# Revit family: ВДО
name_source: partatom
category: Оборудование
units: mm (PartAtom-declared; Revit-internal decimal feet)

## family parameters
Всегда вертикально = Да
Классификация = Нет
На основе рабочей плоскости = Нет
Общий = Нет
При загрузке вырезать с полостями = Нет
Размер круглого соединителя = Использовать диаметр
Тип детали = Нормальный
Точка принадлежности помещению = Нет

## types (239) — shared parameters
00_20_Manufacturer = Вентс
00_20_Name = Осьовий вентилятор димовидалення
Casing Material = Металл, окрашенный, синий, матовый RAL 5007
Grid Material = Cover Grid Cross
Load Classification = HVAC
Maintenance zone material = <По категории>
Number of Fase = 3
Voltage = 400 В
Струм = 0 А
zero-valued in all types: Отметка по умолчанию

## per-type parameters (varying)
| type | 00_20_Type | D1 | D2 | Dn | Dv | Dy | L | Ld | Lv | Maximum Air Flow | N | P | Power | W | W1 | d | l | l1 | n | r1 | Вага | Двигатель |
| ВДО-400-2Д/0,55-6/25/AЛ | ВДО-400-2Д/0,55-6/25/AЛ | 450 мм | 490 мм | 404 мм | 390 мм | 400 мм | 400 мм | 120 мм | 105 мм | 1390.0 л/с | 6 | 240 мм | 550 Вт | 525 мм | 475 мм | 8 мм | 200 мм | -200 мм | 12 | 225 мм | 23.00 кг | Двигатель : Двигатель_0.55 кВт |
| ВДО-1250-4Д/18,5-8/23/AЛ | ВДО-1250-4Д/18,5-8/23/AЛ | 1320 мм | 1400 мм | 1254 мм | 1240 мм | 1250 мм | 750 мм | 225 мм | 210 мм | 21400.0 л/с | 8 | 665 мм | 18500 Вт | 1450 мм | 1400 мм | 15 мм | 375 мм | -375 мм | 20 | 660 мм | 335.00 кг | Двигатель : Двигатель_18.5 кВт |
| ВДО-500-2Д/1,1-6/25/AЛ | ВДО-500-2Д/1,1-6/25/AЛ | 560 мм | 600 мм | 504 мм | 490 мм | 500 мм | 400 мм | 120 мм | 105 мм | 2200.0 л/с | 6 | 290 мм | 1100 Вт | 620 мм | 570 мм | 12 мм | 200 мм | -200 мм | 12 | 280 мм | 32.00 кг | Двигатель : Двигатель_1.1 кВт |
| ВДО-560-2Д/1,1-6/25/AЛ | ВДО-560-2Д/1,1-6/25/AЛ | 620 мм | 660 мм | 564 мм | 550 мм | 560 мм | 400 мм | 120 мм | 105 мм | 2650.0 л/с | 6 | 320 мм | 1100 Вт | 680 мм | 630 мм | 12 мм | 200 мм | -200 мм | 12 | 310 мм | 34.00 кг | Двигатель : Двигатель_1.1 кВт |
| ВДО-450-2Д/0,75-6/25/AЛ | ВДО-450-2Д/0,75-6/25/AЛ | 500 мм | 540 мм | 454 мм | 440 мм | 450 мм | 400 мм | 120 мм | 105 мм | 1800.0 л/с | 6 | 265 мм | 750 Вт | 580 мм | 530 мм | 8 мм | 200 мм | -200 мм | 12 | 250 мм | 26.10 кг | Двигатель : Двигатель_0.75 кВт |
| ВДО-630-2Д/2,2-6/25/AЛ | ВДО-630-2Д/2,2-6/25/AЛ | 620 мм | 690 мм | 634 мм | 620 мм | 630 мм | 400 мм | 120 мм | 105 мм | 3900.0 л/с | 6 | 355 мм | 2200 Вт | 750 мм | 700 мм | 12 мм | 200 мм | -200 мм | 12 | 310 мм | 41.50 кг | Двигатель : Двигатель_2.2 кВт |
| ВДО-710-4Д/0,75-6/20/AЛ | ВДО-710-4Д/0,75-6/20/AЛ | 770 мм | 810 мм | 714 мм | 700 мм | 710 мм | 400 мм | 120 мм | 105 мм | 2900.0 л/с | 6 | 395 мм | 750 Вт | 845 мм | 795 мм | 12 мм | 200 мм | -200 мм | 16 | 385 мм | 47.50 кг | Двигатель : Двигатель_0.75 кВт |
| ВДО-800-4Д/1,1-6/20/AЛ | ВДО-800-4Д/1,1-6/20/AЛ | 860 мм | 900 мм | 804 мм | 790 мм | 800 мм | 400 мм | 120 мм | 105 мм | 3900.0 л/с | 6 | 440 мм | 1100 Вт | 925 мм | 875 мм | 12 мм | 200 мм | -200 мм | 16 | 430 мм | 59.50 кг | Двигатель : Двигатель_1.1 кВт |
| ВДО-900-4Д/3-8/23,5/AЛ | ВДО-900-4Д/3-8/23,5/AЛ | 970 мм | 1015 мм | 904 мм | 890 мм | 900 мм | 550 мм | 165 мм | 150 мм | 6500.0 л/с | 8 | 490 мм | 3000 Вт | 1025 мм | 975 мм | 15 мм | 275 мм | -275 мм | 16 | 485 мм | 92.00 кг | Двигатель : Двигатель_3 кВт |
| ВДО-1000-4Д/5,5-6/24/AЛ | ВДО-1000-4Д/5,5-6/24/AЛ | 1070 мм | 1115 мм | 1004 мм | 990 мм | 1000 мм | 600 мм | 180 мм | 165 мм | 10000.0 л/с | 6 | 540 мм | 5500 Вт | 1140 мм | 1090 мм | 15 мм | 300 мм | -300 мм | 16 | 535 мм | 147.50 кг | Двигатель : Двигатель_5.5 кВт |
| ВДО-1120-4Д/7,5-6/23/AЛ | ВДО-1120-4Д/7,5-6/23/AЛ | 1190 мм | 1270 мм | 1124 мм | 1110 мм | 1120 мм | 600 мм | 180 мм | 165 мм | 13000.0 л/с | 6 | 600 мм | 7500 Вт | 1280 мм | 1230 мм | 15 мм | 300 мм | -300 мм | 20 | 595 мм | 183.00 кг | Двигатель : Двигатель_7.5 кВт |
| ВДО-400-2Д/0,75-6/30/AЛ | ВДО-400-2Д/0,75-6/30/AЛ | 450 мм | 490 мм | 404 мм | 390 мм | 400 мм | 400 мм | 120 мм | 105 мм | 1600.0 л/с | 6 | 240 мм | 750 Вт | 525 мм | 475 мм | 8 мм | 200 мм | -200 мм | 12 | 225 мм | 24.60 кг | Двигатель : Двигатель_0.75 кВт |
| ВДО-400-2Д/1,1-6/35/AЛ | ВДО-400-2Д/1,1-6/35/AЛ | 450 мм | 490 мм | 404 мм | 390 мм | 400 мм | 400 мм | 120 мм | 105 мм | 1850.0 л/с | 6 | 240 мм | 1100 Вт | 525 мм | 475 мм | 8 мм | 200 мм | -200 мм | 12 | 225 мм | 28.60 кг | Двигатель : Двигатель_1.1 кВт |
| ВДО-400-2Д/1,5-6/40/AЛ | ВДО-400-2Д/1,5-6/40/AЛ | 450 мм | 490 мм | 404 мм | 390 мм | 400 мм | 400 мм | 120 мм | 105 мм | 2000.0 л/с | 6 | 240 мм | 1500 Вт | 525 мм | 475 мм | 8 мм | 200 мм | -200 мм | 12 | 225 мм | 30.10 кг | Двигатель : Двигатель_1.5 кВт |
| ВДО-400-2Д/1,5-6/45/AЛ | ВДО-400-2Д/1,5-6/45/AЛ | 450 мм | 490 мм | 404 мм | 390 мм | 400 мм | 400 мм | 120 мм | 105 мм | 2200.0 л/с | 6 | 240 мм | 1500 Вт | 525 мм | 475 мм | 8 мм | 200 мм | -200 мм | 12 | 225 мм | 30.10 кг | Двигатель : Двигатель_1.5 кВт |
| ВДО-400-2Д/2,2-8/45/AЛ | ВДО-400-2Д/2,2-8/45/AЛ | 450 мм | 490 мм | 404 мм | 390 мм | 400 мм | 400 мм | 120 мм | 105 мм | 2300.0 л/с | 8 | 240 мм | 2200 Вт | 525 мм | 475 мм | 8 мм | 200 мм | -200 мм | 12 | 225 мм | 32.60 кг | Двигатель : Двигатель_2.2 кВт |
| ВДО-400-4Д/0,55-6/30/AЛ | ВДО-400-4Д/0,55-6/30/AЛ | 450 мм | 490 мм | 404 мм | 390 мм | 400 мм | 400 мм | 120 мм | 105 мм | 800.0 л/с | 6 | 240 мм | 550 Вт | 525 мм | 475 мм | 8 мм | 200 мм | -200 мм | 12 | 225 мм | 24.50 кг | Двигатель : Двигатель_0.55 кВт |
| ВДО-400-4Д/0,55-6/35/AЛ | ВДО-400-4Д/0,55-6/35/AЛ | 450 мм | 490 мм | 404 мм | 390 мм | 400 мм | 400 мм | 120 мм | 105 мм | 950.0 л/с | 6 | 240 мм | 550 Вт | 525 мм | 475 мм | 8 мм | 200 мм | -200 мм | 12 | 225 мм | 24.50 кг | Двигатель : Двигатель_0.55 кВт |
| ВДО-400-4Д/0,55-6/40/AЛ | ВДО-400-4Д/0,55-6/40/AЛ | 450 мм | 490 мм | 404 мм | 390 мм | 400 мм | 400 мм | 120 мм | 105 мм | 1000.0 л/с | 6 | 240 мм | 550 Вт | 525 мм | 475 мм | 8 мм | 200 мм | -200 мм | 12 | 225 мм | 24.50 кг | Двигатель : Двигатель_0.55 кВт |
| ВДО-400-4Д/0,55-6/45/AЛ | ВДО-400-4Д/0,55-6/45/AЛ | 450 мм | 490 мм | 404 мм | 390 мм | 400 мм | 400 мм | 120 мм | 105 мм | 1050.0 л/с | 6 | 240 мм | 550 Вт | 525 мм | 475 мм | 8 мм | 200 мм | -200 мм | 12 | 225 мм | 24.50 кг | Двигатель : Двигатель_0.55 кВт |
| ВДО-400-4Д/0,55-8/45/AЛ | ВДО-400-4Д/0,55-8/45/AЛ | 450 мм | 490 мм | 404 мм | 390 мм | 400 мм | 400 мм | 120 мм | 105 мм | 1150.0 л/с | 8 | 240 мм | 550 Вт | 525 мм | 475 мм | 8 мм | 200 мм | -200 мм | 12 | 225 мм | 25.00 кг | Двигатель : Двигатель_0.55 кВт |
| ВДО-400-2/4Д/0,8/0,2-6/30/AЛ | ВДО-400-2/4Д/0,8/0,2-6/30/AЛ | 450 мм | 490 мм | 404 мм | 390 мм | 400 мм | 400 мм | 120 мм | 105 мм | 1600.0 л/с | 6 | 240 мм | 800 Вт | 525 мм | 475 мм | 8 мм | 200 мм | -200 мм | 12 | 225 мм | 29.10 кг | Двигатель : Двигатель_0.8 кВт |
| ВДО-400-2/4Д/1,1/0,25-6/35/AЛ | ВДО-400-2/4Д/1,1/0,25-6/35/AЛ | 450 мм | 490 мм | 404 мм | 390 мм | 400 мм | 400 мм | 120 мм | 105 мм | 1850.0 л/с | 6 | 240 мм | 1100 Вт | 525 мм | 475 мм | 8 мм | 200 мм | -200 мм | 12 | 225 мм | 30.10 кг | Двигатель : Двигатель_1.1 кВт |
| ВДО-400-2/4Д/1,5/0,37-6/40/AЛ | ВДО-400-2/4Д/1,5/0,37-6/40/AЛ | 450 мм | 490 мм | 404 мм | 390 мм | 400 мм | 400 мм | 120 мм | 105 мм | 2000.0 л/с | 6 | 240 мм | 1100 Вт | 525 мм | 475 мм | 8 мм | 200 мм | -200 мм | 12 | 225 мм | 35.80 кг | Двигатель : Двигатель_1.5 кВт |
| ВДО-400-2/4Д/1,5/0,37-6/45/AЛ | ВДО-400-2/4Д/1,5/0,37-6/45/AЛ | 450 мм | 490 мм | 404 мм | 390 мм | 400 мм | 400 мм | 120 мм | 105 мм | 2200.0 л/с | 6 | 240 мм | 1500 Вт | 525 мм | 475 мм | 8 мм | 200 мм | -200 мм | 12 | 225 мм | 35.80 кг | Двигатель : Двигатель_1.5 кВт |
| ВДО-400-2/4Д/2,2/0,5-8/45/AЛ | ВДО-400-2/4Д/2,2/0,5-8/45/AЛ | 450 мм | 490 мм | 404 мм | 390 мм | 400 мм | 400 мм | 120 мм | 105 мм | 2250.0 л/с | 8 | 240 мм | 2200 Вт | 525 мм | 475 мм | 8 мм | 200 мм | -200 мм | 12 | 225 мм | 38.00 кг | Двигатель : Двигатель_2.2 кВт |
| ВДО-450-2Д/1,1-6/30/AЛ | ВДО-450-2Д/1,1-6/30/AЛ | 500 мм | 540 мм | 454 мм | 440 мм | 450 мм | 400 мм | 120 мм | 105 мм | 2170.0 л/с | 6 | 265 мм | 1100 Вт | 580 мм | 530 мм | 8 мм | 200 мм | -200 мм | 12 | 250 мм | 30.10 кг | Двигатель : Двигатель_1.1 кВт |
| ВДО-450-2Д/1,5-6/35/AЛ | ВДО-450-2Д/1,5-6/35/AЛ | 500 мм | 540 мм | 454 мм | 440 мм | 450 мм | 400 мм | 120 мм | 105 мм | 2600.0 л/с | 6 | 265 мм | 1500 Вт | 580 мм | 530 мм | 8 мм | 200 мм | -200 мм | 12 | 250 мм | 31.60 кг | Двигатель : Двигатель_1.5 кВт |
| ВДО-450-2Д/2,2-6/40/AЛ | ВДО-450-2Д/2,2-6/40/AЛ | 500 мм | 540 мм | 454 мм | 440 мм | 450 мм | 400 мм | 120 мм | 105 мм | 2800.0 л/с | 6 | 265 мм | 2200 Вт | 580 мм | 530 мм | 8 мм | 200 мм | -200 мм | 12 | 250 мм | 34.00 кг | Двигатель : Двигатель_2.2 кВт |
| ВДО-450-2Д/3-8/40/AЛ | ВДО-450-2Д/3-8/40/AЛ | 500 мм | 540 мм | 454 мм | 440 мм | 450 мм | 400 мм | 120 мм | 105 мм | 2900.0 л/с | 6 | 265 мм | 3000 Вт | 580 мм | 530 мм | 8 мм | 200 мм | -200 мм | 12 | 250 мм | 34.00 кг | Двигатель : Двигатель_3 кВт |
| ВДО-450-2Д/4-8/45/AЛ | ВДО-450-2Д/4-8/45/AЛ | 500 мм | 540 мм | 454 мм | 440 мм | 450 мм | 400 мм | 120 мм | 105 мм | 3300.0 л/с | 8 | 265 мм | 4000 Вт | 580 мм | 530 мм | 8 мм | 200 мм | -200 мм | 12 | 250 мм | 52.80 кг | Двигатель : Двигатель_3 кВт |
| ВДО-450-4Д/0,55-6/25/AЛ | ВДО-450-2Д/3-8/40/AЛ | 500 мм | 540 мм | 454 мм | 440 мм | 450 мм | 400 мм | 120 мм | 105 мм | 640.0 л/с | 6 | 265 мм | 550 Вт | 580 мм | 530 мм | 8 мм | 200 мм | -200 мм | 12 | 250 мм | 24.60 кг | Двигатель : Двигатель_0.55 кВт |
| ВДО-450-4Д/0,55-6/30/AЛ | ВДО-450-4Д/0,55-6/30/AЛ | 500 мм | 540 мм | 454 мм | 440 мм | 450 мм | 400 мм | 120 мм | 105 мм | 1050.0 л/с | 6 | 265 мм | 550 Вт | 580 мм | 530 мм | 8 мм | 200 мм | -200 мм | 12 | 250 мм | 24.60 кг | Двигатель : Двигатель_0.55 кВт |
| ВДО-450-4Д/0,55-6/35/AЛ | ВДО-450-4Д/0,55-6/35/AЛ | 500 мм | 540 мм | 454 мм | 440 мм | 450 мм | 400 мм | 120 мм | 105 мм | 1250.0 л/с | 6 | 265 мм | 550 Вт | 580 мм | 530 мм | 8 мм | 200 мм | -200 мм | 12 | 250 мм | 24.60 кг | Двигатель : Двигатель_0.55 кВт |
| ВДО-450-4Д/0,55-6/40/AЛ | ВДО-450-4Д/0,55-6/40/AЛ | 500 мм | 540 мм | 454 мм | 440 мм | 450 мм | 400 мм | 120 мм | 105 мм | 1400.0 л/с | 6 | 265 мм | 550 Вт | 580 мм | 530 мм | 8 мм | 200 мм | -200 мм | 12 | 250 мм | 24.60 кг | Двигатель : Двигатель_0.55 кВт |
| ВДО-450-4Д/0,55-8/40/AЛ | ВДО-450-4Д/0,55-8/40/AЛ | 500 мм | 540 мм | 454 мм | 440 мм | 450 мм | 400 мм | 120 мм | 105 мм | 1450.0 л/с | 8 | 265 мм | 550 Вт | 580 мм | 530 мм | 8 мм | 200 мм | -200 мм | 12 | 250 мм | 24.60 кг | Двигатель : Двигатель_0.55 кВт |
| ВДО-450-4Д/0,55-8/45/AЛ | ВДО-450-4Д/0,55-8/45/AЛ | 500 мм | 540 мм | 454 мм | 440 мм | 450 мм | 400 мм | 120 мм | 105 мм | 1650.0 л/с | 8 | 265 мм | 550 Вт | 580 мм | 530 мм | 8 мм | 200 мм | -200 мм | 12 | 250 мм | 24.60 кг | Двигатель : Двигатель_0.55 кВт |
| ВДО-450-2/4Д/4,4/1,1-8/45/AЛ | ВДО-450-2/4Д/4,4/1,1-8/45/AЛ | 500 мм | 540 мм | 454 мм | 440 мм | 450 мм | 400 мм | 120 мм | 105 мм | 3300.0 л/с | 8 | 265 мм | 4400 Вт | 580 мм | 530 мм | 8 мм | 200 мм | -200 мм | 12 | 250 мм | 63.80 кг | Двигатель : Двигатель_4.4 кВт |
| ВДО-450-2/4Д/3,1/0,8-8/40/AЛ | ВДО-450-2/4Д/3,1/0,8-8/40/AЛ | 500 мм | 540 мм | 454 мм | 440 мм | 450 мм | 400 мм | 120 мм | 105 мм | 2900.0 л/с | 8 | 265 мм | 3100 Вт | 580 мм | 530 мм | 8 мм | 200 мм | -200 мм | 12 | 250 мм | 51.90 кг | Двигатель : Двигатель_3.1 кВт |
| ВДО-450-2/4Д/2,2/0,5-6/40/AЛ | ВДО-450-2/4Д/2,2/0,5-6/40/AЛ | 500 мм | 540 мм | 454 мм | 440 мм | 450 мм | 400 мм | 120 мм | 105 мм | 2800.0 л/с | 6 | 265 мм | 2200 Вт | 580 мм | 530 мм | 8 мм | 200 мм | -200 мм | 12 | 250 мм | 39.30 кг | Двигатель : Двигатель_2.2 кВт |
| ВДО-450-2/4Д/1,5/0,37-6/35/AЛ | ВДО-450-2/4Д/1,5/0,37-6/35/AЛ | 500 мм | 540 мм | 454 мм | 440 мм | 450 мм | 400 мм | 120 мм | 105 мм | 2500.0 л/с | 6 | 265 мм | 1500 Вт | 580 мм | 530 мм | 8 мм | 200 мм | -200 мм | 12 | 250 мм | 37.30 кг | Двигатель : Двигатель_1.5 кВт |
| ВДО-450-2/4Д/1,1/0,25-6/30/AЛ | ВДО-450-2/4Д/1,1/0,25-6/30/AЛ | 500 мм | 540 мм | 454 мм | 440 мм | 450 мм | 400 мм | 120 мм | 105 мм | 2150.0 л/с | 6 | 265 мм | 1100 Вт | 580 мм | 530 мм | 8 мм | 200 мм | -200 мм | 12 | 250 мм | 31.60 кг | Двигатель : Двигатель_1.1 кВт |
| ВДО-450-2/4Д/0,8/0,2-6/25/AЛ | ВДО-450-2/4Д/0,8/0,2-6/25/AЛ | 500 мм | 540 мм | 454 мм | 440 мм | 450 мм | 400 мм | 120 мм | 105 мм | 1800.0 л/с | 6 | 265 мм | 800 Вт | 580 мм | 530 мм | 8 мм | 200 мм | -200 мм | 12 | 250 мм | 30.60 кг | Двигатель : Двигатель_0.8 кВт |
| ВДО-500-2Д/1,5-6/30/AЛ | ВДО-500-2Д/1,5-6/30/AЛ | 560 мм | 600 мм | 504 мм | 490 мм | 500 мм | 400 мм | 120 мм | 105 мм | 2650.0 л/с | 6 | 290 мм | 1500 Вт | 620 мм | 570 мм | 12 мм | 200 мм | -200 мм | 12 | 280 мм | 33.50 кг | Двигатель : Двигатель_1.5 кВт |
| ВДО-500-2Д/2,2-6/35/AЛ | ВДО-500-2Д/2,2-6/35/AЛ | 560 мм | 600 мм | 504 мм | 490 мм | 500 мм | 400 мм | 120 мм | 105 мм | 3200.0 л/с | 6 | 290 мм | 2200 Вт | 620 мм | 570 мм | 12 мм | 200 мм | -200 мм | 12 | 280 мм | 36.00 кг | Двигатель : Двигатель_2.2 кВт |
| ВДО-500-2Д/3-8/35/AЛ | ВДО-500-2Д/3-8/35/AЛ | 560 мм | 600 мм | 504 мм | 490 мм | 500 мм | 400 мм | 120 мм | 105 мм | 3500.0 л/с | 8 | 290 мм | 3000 Вт | 620 мм | 570 мм | 12 мм | 200 мм | -200 мм | 12 | 280 мм | 43.00 кг | Двигатель : Двигатель_3 кВт |
| ВДО-500-2Д/4-8/40/AЛ | ВДО-500-2Д/4-8/40/AЛ | 560 мм | 600 мм | 504 мм | 490 мм | 500 мм | 500 мм | 150 мм | 135 мм | 3900.0 л/с | 8 | 290 мм | 4000 Вт | 620 мм | 570 мм | 12 мм | 250 мм | -250 мм | 12 | 280 мм | 55.00 кг | Двигатель : Двигатель_4 кВт |
| ВДО-500-2Д/5,5-8/45/AЛ | ВДО-500-2Д/5,5-8/45/AЛ | 560 мм | 600 мм | 504 мм | 490 мм | 500 мм | 500 мм | 150 мм | 135 мм | 4300.0 л/с | 8 | 290 мм | 5500 Вт | 620 мм | 570 мм | 12 мм | 250 мм | -250 мм | 12 | 280 мм | 63.00 кг | Двигатель : Двигатель_5.5 кВт |
| ВДО-500-4Д/0,55-6/25/AЛ | ВДО-500-4Д/0,55-6/25/AЛ | 560 мм | 600 мм | 504 мм | 490 мм | 500 мм | 400 мм | 120 мм | 105 мм | 1100.0 л/с | 6 | 290 мм | 550 Вт | 620 мм | 570 мм | 12 мм | 200 мм | -200 мм | 12 | 280 мм | 28.00 кг | Двигатель : Двигатель_0.55 кВт |
| ВДО-500-4Д/0,55-6/30/AЛ | ВДО-500-4Д/0,55-6/30/AЛ | 560 мм | 600 мм | 504 мм | 490 мм | 500 мм | 400 мм | 120 мм | 105 мм | 1350.0 л/с | 6 | 290 мм | 550 Вт | 620 мм | 570 мм | 12 мм | 200 мм | -200 мм | 12 | 280 мм | 28.00 кг | Двигатель : Двигатель_0.55 кВт |
| ВДО-500-4Д/0,55-6/35/AЛ | ВДО-500-4Д/0,55-6/35/AЛ | 560 мм | 600 мм | 504 мм | 490 мм | 500 мм | 400 мм | 120 мм | 105 мм | 1650.0 л/с | 6 | 290 мм | 550 Вт | 620 мм | 570 мм | 12 мм | 200 мм | -200 мм | 12 | 280 мм | 28.00 кг | Двигатель : Двигатель_0.55 кВт |
| ВДО-500-4Д/0,55-6/40/AЛ | ВДО-500-4Д/0,55-6/40/AЛ | 560 мм | 600 мм | 504 мм | 490 мм | 500 мм | 400 мм | 120 мм | 105 мм | 1780.0 л/с | 6 | 290 мм | 550 Вт | 620 мм | 570 мм | 12 мм | 200 мм | -200 мм | 12 | 280 мм | 28.00 кг | Двигатель : Двигатель_0.55 кВт |
| ВДО-500-4Д/0,55-6/45/AЛ | ВДО-500-4Д/0,55-6/45/AЛ | 560 мм | 600 мм | 504 мм | 490 мм | 500 мм | 400 мм | 120 мм | 105 мм | 1950.0 л/с | 6 | 290 мм | 550 Вт | 620 мм | 570 мм | 12 мм | 200 мм | -200 мм | 12 | 280 мм | 28.00 кг | Двигатель : Двигатель_0.55 кВт |
| ВДО-500-4Д/0,75-8/45/AЛ | ВДО-500-4Д/0,75-8/45/AЛ | 560 мм | 600 мм | 504 мм | 490 мм | 500 мм | 400 мм | 120 мм | 105 мм | 2100.0 л/с | 8 | 290 мм | 750 Вт | 620 мм | 570 мм | 12 мм | 200 мм | -200 мм | 12 | 280 мм | 29.50 кг | Двигатель : Двигатель_0.75 кВт |
| ВДО-500-2/4Д/1,1/0,25-6/25/AЛ | ВДО-500-2/4Д/1,1/0,25-6/25/AЛ | 560 мм | 600 мм | 504 мм | 490 мм | 500 мм | 400 мм | 120 мм | 105 мм | 2200.0 л/с | 6 | 290 мм | 1100 Вт | 620 мм | 570 мм | 12 мм | 200 мм | -200 мм | 12 | 280 мм | 29.50 кг | Двигатель : Двигатель_1.1 кВт |
| ВДО-500-2/4Д/1,5/0,37-6/30/AЛ | ВДО-500-2/4Д/1,5/0,37-6/30/AЛ | 560 мм | 600 мм | 504 мм | 490 мм | 500 мм | 400 мм | 120 мм | 105 мм | 2650.0 л/с | 6 | 290 мм | 1500 Вт | 620 мм | 570 мм | 12 мм | 200 мм | -200 мм | 12 | 280 мм | 39.00 кг | Двигатель : Двигатель_1.5 кВт |
| ВДО-500-2/4Д/2,2/0,5-6/35/AЛ | ВДО-500-2/4Д/2,2/0,5-6/35/AЛ | 560 мм | 600 мм | 504 мм | 490 мм | 500 мм | 400 мм | 120 мм | 105 мм | 3200.0 л/с | 6 | 290 мм | 2200 Вт | 620 мм | 570 мм | 12 мм | 200 мм | -200 мм | 12 | 280 мм | 41.00 кг | Двигатель : Двигатель_2.2 кВт |
| ВДО-500-2/4Д/3,1/0,8-8/35/AЛ | ВДО-500-2/4Д/3,1/0,8-8/35/AЛ | 560 мм | 600 мм | 504 мм | 490 мм | 500 мм | 500 мм | 150 мм | 135 мм | 3600.0 л/с | 8 | 290 мм | 3100 Вт | 620 мм | 570 мм | 12 мм | 250 мм | -250 мм | 12 | 280 мм | 54.00 кг | Двигатель : Двигатель_3.1 кВт |
| ВДО-500-2/4Д/4,4/1,1-8/40/AЛ | ВДО-500-2/4Д/4,4/1,1-8/40/AЛ | 560 мм | 600 мм | 504 мм | 490 мм | 500 мм | 500 мм | 150 мм | 135 мм | 3900.0 л/с | 8 | 290 мм | 4400 Вт | 620 мм | 570 мм | 12 мм | 250 мм | -250 мм | 12 | 280 мм | 66.00 кг | Двигатель : Двигатель_4.4 кВт |
| ВДО-500-2/4Д/6/1,5-8/45/AЛ | ВДО-500-2/4Д/6/1,5-8/45/AЛ | 560 мм | 600 мм | 504 мм | 490 мм | 500 мм | 550 мм | 165 мм | 150 мм | 4300.0 л/с | 8 | 290 мм | 6000 Вт | 620 мм | 570 мм | 12 мм | 275 мм | -275 мм | 12 | 280 мм | 85.00 кг | Двигатель : Двигатель_6 кВт |
| ВДО-560-2Д/1,5-6/30/AЛ | ВДО-560-2Д/1,5-6/30/AЛ | 620 мм | 660 мм | 564 мм | 550 мм | 560 мм | 400 мм | 120 мм | 105 мм | 3300.0 л/с | 6 | 320 мм | 1500 Вт | 680 мм | 630 мм | 12 мм | 200 мм | -200 мм | 12 | 310 мм | 35.50 кг | Двигатель : Двигатель_1.5 кВт |
| ВДО-560-2Д/2,2-8/30/AЛ | ВДО-560-2Д/2,2-8/30/AЛ | 620 мм | 660 мм | 564 мм | 550 мм | 560 мм | 400 мм | 120 мм | 105 мм | 3750.0 л/с | 8 | 320 мм | 2200 Вт | 680 мм | 630 мм | 12 мм | 200 мм | -200 мм | 12 | 310 мм | 38.00 кг | Двигатель : Двигатель_2.2 кВт |
| ВДО-560-2Д/4-8/35/AЛ | ВДО-560-2Д/4-8/35/AЛ | 620 мм | 660 мм | 564 мм | 550 мм | 560 мм | 500 мм | 150 мм | 135 мм | 4580.0 л/с | 8 | 320 мм | 4000 Вт | 680 мм | 630 мм | 12 мм | 250 мм | -250 мм | 12 | 310 мм | 57.50 кг | Двигатель : Двигатель_4 кВт |
| ВДО-560-2Д/5,5-8/40/AЛ | ВДО-560-2Д/5,5-8/40/AЛ | 620 мм | 660 мм | 564 мм | 550 мм | 560 мм | 500 мм | 150 мм | 135 мм | 5000.0 л/с | 8 | 320 мм | 5500 Вт | 680 мм | 630 мм | 12 мм | 250 мм | -250 мм | 12 | 310 мм | 65.50 кг | Двигатель : Двигатель_5.5 кВт |
| ВДО-560-2Д/7,5-8/45/AЛ | ВДО-560-2Д/7,5-8/45/AЛ | 620 мм | 660 мм | 564 мм | 550 мм | 560 мм | 500 мм | 150 мм | 135 мм | 5700.0 л/с | 8 | 320 мм | 7500 Вт | 680 мм | 630 мм | 12 мм | 250 мм | -250 мм | 12 | 310 мм | 67.50 кг | Двигатель : Двигатель_7.5 кВт |
| ВДО-560-4Д/0,55-6/25/AЛ | ВДО-560-4Д/0,55-6/25/AЛ | 620 мм | 660 мм | 564 мм | 550 мм | 560 мм | 400 мм | 120 мм | 105 мм | 1350.0 л/с | 6 | 320 мм | 550 Вт | 680 мм | 630 мм | 12 мм | 200 мм | -200 мм | 12 | 310 мм | 30.00 кг | Двигатель : Двигатель_0.55 кВт |
| ВДО-560-4Д/0,55-6/30/AЛ | ВДО-560-4Д/0,55-6/30/AЛ | 620 мм | 660 мм | 564 мм | 550 мм | 560 мм | 400 мм | 120 мм | 105 мм | 1650.0 л/с | 6 | 320 мм | 550 Вт | 680 мм | 630 мм | 12 мм | 200 мм | -200 мм | 12 | 310 мм | 30.00 кг | Двигатель : Двигатель_0.55 кВт |
| ВДО-560-4Д/0,55-6/35/AЛ | ВДО-560-4Д/0,55-6/35/AЛ | 620 мм | 660 мм | 564 мм | 550 мм | 560 мм | 400 мм | 120 мм | 105 мм | 2050.0 л/с | 6 | 320 мм | 550 Вт | 680 мм | 630 мм | 12 мм | 200 мм | -200 мм | 12 | 310 мм | 30.00 кг | Двигатель : Двигатель_0.55 кВт |
| ВДО-560-4Д/0,55-6/40/AЛ | ВДО-560-4Д/0,55-6/40/AЛ | 620 мм | 660 мм | 564 мм | 550 мм | 560 мм | 400 мм | 120 мм | 105 мм | 2300.0 л/с | 6 | 320 мм | 550 Вт | 680 мм | 630 мм | 12 мм | 200 мм | -200 мм | 12 | 310 мм | 30.00 кг | Двигатель : Двигатель_0.55 кВт |
| ВДО-560-4Д/0,55-6/45/AЛ | ВДО-560-4Д/0,55-6/45/AЛ | 620 мм | 660 мм | 564 мм | 550 мм | 560 мм | 400 мм | 120 мм | 105 мм | 2500.0 л/с | 6 | 320 мм | 550 Вт | 680 мм | 630 мм | 12 мм | 200 мм | -200 мм | 12 | 310 мм | 30.00 кг | Двигатель : Двигатель_0.55 кВт |
| ВДО-560-4Д/0,75-8/45/AЛ | ВДО-560-4Д/0,75-8/45/AЛ | 620 мм | 660 мм | 564 мм | 550 мм | 560 мм | 400 мм | 120 мм | 105 мм | 2850.0 л/с | 8 | 320 мм | 750 Вт | 680 мм | 630 мм | 12 мм | 200 мм | -200 мм | 12 | 310 мм | 31.50 кг | Двигатель : Двигатель_0.75 кВт |
| ВДО-560-2/4Д/1,1/0,25-6/25/AЛ | ВДО-560-2/4Д/1,1/0,25-6/25/AЛ | 620 мм | 660 мм | 564 мм | 550 мм | 560 мм | 400 мм | 120 мм | 105 мм | 2700.0 л/с | 6 | 320 мм | 1100 Вт | 680 мм | 630 мм | 12 мм | 200 мм | -200 мм | 12 | 310 мм | 35.50 кг | Двигатель : Двигатель_1.1 кВт |
| ВДО-560-2/4Д/1,5/0,37-6/30/AЛ | ВДО-560-2/4Д/1,5/0,37-6/30/AЛ | 620 мм | 660 мм | 564 мм | 550 мм | 560 мм | 400 мм | 120 мм | 105 мм | 3300.0 л/с | 6 | 320 мм | 1500 Вт | 680 мм | 630 мм | 12 мм | 200 мм | -200 мм | 12 | 310 мм | 41.00 кг | Двигатель : Двигатель_1.5 кВт |
| ВДО-560-2/4Д/2,2/0,5-8/30/AЛ | ВДО-560-2/4Д/2,2/0,5-8/30/AЛ | 620 мм | 660 мм | 564 мм | 550 мм | 560 мм | 400 мм | 120 мм | 105 мм | 3750.0 л/с | 8 | 320 мм | 2200 Вт | 680 мм | 630 мм | 12 мм | 200 мм | -200 мм | 12 | 310 мм | 43.50 кг | Двигатель : Двигатель_2.2 кВт |
| ВДО-560-2/4Д/4,4/1,1-8/35/AЛ | ВДО-560-2/4Д/4,4/1,1-8/35/AЛ | 620 мм | 660 мм | 564 мм | 550 мм | 560 мм | 500 мм | 150 мм | 135 мм | 4600.0 л/с | 8 | 320 мм | 4400 Вт | 680 мм | 630 мм | 12 мм | 250 мм | -250 мм | 12 | 310 мм | 68.50 кг | Двигатель : Двигатель_4.4 кВт |
| ВДО-560-2/4Д/6/1,5-8/40/AЛ | ВДО-560-2/4Д/6/1,5-8/40/AЛ | 620 мм | 660 мм | 564 мм | 550 мм | 560 мм | 550 мм | 165 мм | 150 мм | 5000.0 л/с | 8 | 320 мм | 6000 Вт | 680 мм | 630 мм | 12 мм | 275 мм | -275 мм | 12 | 310 мм | 96.50 кг | Двигатель : Двигатель_6 кВт |
| ВДО-560-2/4Д/8/2-8/45/AЛ | ВДО-560-2/4Д/8/2-8/45/AЛ | 620 мм | 660 мм | 564 мм | 550 мм | 560 мм | 550 мм | 165 мм | 150 мм | 5700.0 л/с | 8 | 320 мм | 8000 Вт | 680 мм | 630 мм | 12 мм | 275 мм | -275 мм | 12 | 310 мм | 105.50 кг | Двигатель : Двигатель_8 кВт |
| ВДО-630-2Д/3-6/30/AЛ | ВДО-630-2Д/3-6/30/AЛ | 620 мм | 690 мм | 634 мм | 620 мм | 630 мм | 400 мм | 120 мм | 105 мм | 4700.0 л/с | 6 | 355 мм | 3000 Вт | 750 мм | 700 мм | 12 мм | 200 мм | -200 мм | 12 | 310 мм | 48.00 кг | Двигатель : Двигатель_3 кВт |
| ВДО-630-2Д/4-7/32,5/AЛ | ВДО-630-2Д/4-7/32,5/AЛ | 620 мм | 690 мм | 634 мм | 620 мм | 630 мм | 500 мм | 150 мм | 135 мм | 5250.0 л/с | 7 | 355 мм | 4000 Вт | 750 мм | 700 мм | 12 мм | 250 мм | -250 мм | 12 | 310 мм | 61.50 кг | Двигатель : Двигатель_4 кВт |
| ВДО-630-2Д/5,5-7/35/AЛ | ВДО-630-2Д/5,5-7/35/AЛ | 620 мм | 690 мм | 634 мм | 620 мм | 630 мм | 500 мм | 150 мм | 135 мм | 5850.0 л/с | 7 | 355 мм | 5500 Вт | 750 мм | 700 мм | 12 мм | 250 мм | -250 мм | 12 | 310 мм | 70.00 кг | Двигатель : Двигатель_5.5 кВт |
| ВДО-630-2Д/5,5-7/37,5/AЛ | ВДО-630-2Д/5,5-7/37,5/AЛ | 620 мм | 690 мм | 634 мм | 620 мм | 630 мм | 500 мм | 150 мм | 135 мм | 6100.0 л/с | 7 | 355 мм | 5500 Вт | 750 мм | 700 мм | 12 мм | 250 мм | -250 мм | 12 | 310 мм | 70.00 кг | Двигатель : Двигатель_5.5 кВт |
| ВДО-630-2Д/7,5-7/41,5/AЛ | ВДО-630-2Д/7,5-7/41,5/AЛ | 620 мм | 690 мм | 634 мм | 620 мм | 630 мм | 500 мм | 150 мм | 135 мм | 6100.0 л/с | 7 | 355 мм | 7500 Вт | 750 мм | 700 мм | 12 мм | 250 мм | -250 мм | 12 | 310 мм | 71.50 кг | Двигатель : Двигатель_7.5 кВт |
| ВДО-630-2Д/11-8/41,5/AЛ | ВДО-630-2Д/11-8/41,5/AЛ | 620 мм | 690 мм | 634 мм | 620 мм | 630 мм | 550 мм | 165 мм | 150 мм | 7250.0 л/с | 8 | 355 мм | 11000 Вт | 750 мм | 700 мм | 12 мм | 275 мм | -275 мм | 12 | 310 мм | 119.50 кг | Двигатель : Двигатель_11 кВт |
| ВДО-630-2Д/15-8/46,5/AЛ | ВДО-630-2Д/15-8/46,5/AЛ | 620 мм | 690 мм | 634 мм | 620 мм | 630 мм | 700 мм | 210 мм | 195 мм | 8000.0 л/с | 8 | 355 мм | 15000 Вт | 750 мм | 700 мм | 12 мм | 350 мм | -350 мм | 12 | 310 мм | 167.00 кг | Двигатель : Двигатель_15 кВт |
| ВДО-630-2Д/15-9/48,5/AЛ | ВДО-630-2Д/15-9/48,5/AЛ | 620 мм | 690 мм | 634 мм | 620 мм | 630 мм | 700 мм | 210 мм | 195 мм | 8350.0 л/с | 9 | 355 мм | 15000 Вт | 750 мм | 700 мм | 12 мм | 350 мм | -350 мм | 12 | 310 мм | 166.00 кг | Двигатель : Двигатель_15 кВт |
| ВДО-630-4Д/0,55-8/25/AЛ | ВДО-630-4Д/0,55-8/25/AЛ | 620 мм | 690 мм | 634 мм | 620 мм | 630 мм | 400 мм | 120 мм | 105 мм | 1800.0 л/с | 8 | 355 мм | 550 Вт | 750 мм | 700 мм | 12 мм | 200 мм | -200 мм | 12 | 310 мм | 31.50 кг | Двигатель : Двигатель_0.55 кВт |
| ВДО-630-4Д/0,55-8/30/AЛ | ВДО-630-4Д/0,55-8/30/AЛ | 620 мм | 690 мм | 634 мм | 620 мм | 630 мм | 400 мм | 120 мм | 105 мм | 2300.0 л/с | 8 | 355 мм | 550 Вт | 750 мм | 700 мм | 12 мм | 200 мм | -200 мм | 12 | 310 мм | 31.50 кг | Двигатель : Двигатель_0.55 кВт |
| ВДО-630-4Д/0,75-8/35/AЛ | ВДО-630-4Д/0,75-8/35/AЛ | 620 мм | 690 мм | 634 мм | 620 мм | 630 мм | 400 мм | 120 мм | 105 мм | 2850.0 л/с | 8 | 355 мм | 750 Вт | 750 мм | 700 мм | 12 мм | 200 мм | -200 мм | 12 | 310 мм | 32.50 кг | Двигатель : Двигатель_0.75 кВт |
| ВДО-630-4Д/1,1-8/40/AЛ | ВДО-630-4Д/1,1-8/40/AЛ | 620 мм | 690 мм | 634 мм | 620 мм | 630 мм | 400 мм | 120 мм | 105 мм | 3200.0 л/с | 8 | 355 мм | 1100 Вт | 750 мм | 700 мм | 12 мм | 200 мм | -200 мм | 12 | 310 мм | 36.50 кг | Двигатель : Двигатель_1.1 кВт |
| ВДО-630-4Д/1,1-6/32,5/AЛ | ВДО-630-4Д/1,1-6/32,5/AЛ | 620 мм | 690 мм | 634 мм | 620 мм | 630 мм | 400 мм | 120 мм | 105 мм | 3550.0 л/с | 6 | 355 мм | 1100 Вт | 750 мм | 700 мм | 12 мм | 200 мм | -200 мм | 12 | 310 мм | 38.50 кг | Двигатель : Двигатель_1.1 кВт |
| ВДО-630-4Д/1,5-6/37,5/AЛ | ВДО-630-4Д/1,5-6/37,5/AЛ | 620 мм | 690 мм | 634 мм | 620 мм | 630 мм | 400 мм | 120 мм | 105 мм | 3900.0 л/с | 6 | 355 мм | 1500 Вт | 750 мм | 700 мм | 12 мм | 200 мм | -200 мм | 12 | 310 мм | 42.50 кг | Двигатель : Двигатель_1.5 кВт |
| ВДО-630-4Д/2,2-6/45/AЛ | ВДО-630-4Д/2,2-6/45/AЛ | 620 мм | 690 мм | 634 мм | 620 мм | 630 мм | 400 мм | 120 мм | 105 мм | 4350.0 л/с | 6 | 355 мм | 2200 Вт | 750 мм | 700 мм | 12 мм | 200 мм | -200 мм | 12 | 310 мм | 48.50 кг | Двигатель : Двигатель_2.2 кВт |
| ВДО-630-2/4Д/2,2/0,5-6/25/AЛ | ВДО-630-2/4Д/2,2/0,5-6/25/AЛ | 620 мм | 690 мм | 634 мм | 620 мм | 630 мм | 400 мм | 120 мм | 105 мм | 3850.0 л/с | 6 | 355 мм | 2200 Вт | 750 мм | 700 мм | 12 мм | 200 мм | -200 мм | 12 | 310 мм | 46.50 кг | Двигатель : Двигатель_2.2 кВт |
| ВДО-630-2/4Д/3,1/0,8-6/30/AЛ | ВДО-630-2/4Д/3,1/0,8-6/30/AЛ | 620 мм | 690 мм | 634 мм | 620 мм | 630 мм | 500 мм | 150 мм | 135 мм | 4700.0 л/с | 6 | 355 мм | 3100 Вт | 750 мм | 700 мм | 12 мм | 250 мм | -250 мм | 12 | 310 мм | 60.00 кг | Двигатель : Двигатель_3.1 кВт |
| ВДО-630-2/4Д/4,4/1,1-7/32,5/AЛ | ВДО-630-2/4Д/4,4/1,1-7/32,5/AЛ | 620 мм | 690 мм | 634 мм | 620 мм | 630 мм | 500 мм | 150 мм | 135 мм | 5150.0 л/с | 7 | 355 мм | 4400 Вт | 750 мм | 700 мм | 12 мм | 250 мм | -250 мм | 12 | 310 мм | 72.50 кг | Двигатель : Двигатель_4.4 кВт |
| ВДО-630-2/4Д/6/1,5-7/35/AЛ | ВДО-630-2/4Д/6/1,5-7/35/AЛ | 620 мм | 690 мм | 634 мм | 620 мм | 630 мм | 550 мм | 165 мм | 150 мм | 5850.0 л/с | 7 | 355 мм | 6000 Вт | 750 мм | 700 мм | 12 мм | 275 мм | -275 мм | 12 | 310 мм | 102.00 кг | Двигатель : Двигатель_6 кВт |
| ВДО-630-2/4Д/6/1,5-7/37,5/AЛ | ВДО-630-2/4Д/6/1,5-7/37,5/AЛ | 620 мм | 690 мм | 634 мм | 620 мм | 630 мм | 550 мм | 165 мм | 150 мм | 6100.0 л/с | 7 | 355 мм | 6000 Вт | 750 мм | 700 мм | 12 мм | 275 мм | -275 мм | 12 | 310 мм | 102.00 кг | Двигатель : Двигатель_6 кВт |
| ВДО-630-2/4Д/8/2-7/41,5/AЛ | ВДО-630-2/4Д/8/2-7/41,5/AЛ | 620 мм | 690 мм | 634 мм | 620 мм | 630 мм | 550 мм | 165 мм | 150 мм | 6700.0 л/с | 7 | 355 мм | 8000 Вт | 750 мм | 700 мм | 12 мм | 275 мм | -275 мм | 12 | 310 мм | 111.00 кг | Двигатель : Двигатель_8 кВт |
| ВДО-630-2/4Д/12/3-8/41,5/AЛ | ВДО-630-2/4Д/12/3-8/41,5/AЛ | 620 мм | 690 мм | 634 мм | 620 мм | 630 мм | 700 мм | 210 мм | 195 мм | 7250.0 л/с | 8 | 355 мм | 12000 Вт | 750 мм | 700 мм | 12 мм | 350 мм | -350 мм | 12 | 310 мм | 177.00 кг | Двигатель : Двигатель_12 кВт |
| ВДО-630-2/4Д/16/4-8/46,5/AЛ | ВДО-630-2/4Д/16/4-8/46,5/AЛ | 620 мм | 690 мм | 634 мм | 620 мм | 630 мм | 700 мм | 210 мм | 195 мм | 7800.0 л/с | 8 | 355 мм | 16000 Вт | 750 мм | 700 мм | 12 мм | 350 мм | -350 мм | 12 | 310 мм | 194.00 кг | Двигатель : Двигатель_16 кВт |
| ВДО-630-2/4Д/16/4-9/48,5/AЛ | ВДО-630-2/4Д/16/4-9/48,5/AЛ | 620 мм | 690 мм | 634 мм | 620 мм | 630 мм | 700 мм | 210 мм | 195 мм | 8350.0 л/с | 9 | 355 мм | 16000 Вт | 750 мм | 700 мм | 12 мм | 350 мм | -350 мм | 12 | 310 мм | 195.00 кг | Двигатель : Двигатель_16 кВт |
| ВДО-630-4/6Д/0,55/0,2-8/25/AЛ | ВДО-630-4/6Д/0,55/0,2-8/25/AЛ | 620 мм | 690 мм | 634 мм | 620 мм | 630 мм | 400 мм | 120 мм | 105 мм | 1800.0 л/с | 8 | 355 мм | 5500 Вт | 750 мм | 700 мм | 12 мм | 200 мм | -200 мм | 12 | 310 мм | 34.00 кг | Двигатель : Двигатель_0.55 кВт |
| ВДО-630-4/6Д/0,55/0,2-8/30/AЛ | ВДО-630-4/6Д/0,55/0,2-8/30/AЛ | 620 мм | 690 мм | 634 мм | 620 мм | 630 мм | 400 мм | 120 мм | 105 мм | 2200.0 л/с | 8 | 355 мм | 5500 Вт | 750 мм | 700 мм | 12 мм | 200 мм | -200 мм | 12 | 310 мм | 34.00 кг | Двигатель : Двигатель_0.55 кВт |
| ВДО-630-4/6Д/0,75/0,25-8/35/AЛ | ВДО-630-4/6Д/0,75/0,25-8/35/AЛ | 620 мм | 690 мм | 634 мм | 620 мм | 630 мм | 400 мм | 120 мм | 105 мм | 2800.0 л/с | 8 | 355 мм | 7500 Вт | 750 мм | 700 мм | 12 мм | 200 мм | -200 мм | 12 | 310 мм | 34.00 кг | Двигатель : Двигатель_0.75 кВт |
| ВДО-630-4/6Д/1,1/0,3-8/40/AЛ | ВДО-630-4/6Д/1,1/0,3-8/40/AЛ | 620 мм | 690 мм | 634 мм | 620 мм | 630 мм | 400 мм | 120 мм | 105 мм | 3200.0 л/с | 8 | 355 мм | 1100 Вт | 750 мм | 700 мм | 12 мм | 200 мм | -200 мм | 12 | 310 мм | 39.50 кг | Двигатель : Двигатель_1.1 кВт |
| ВДО-630-4/6Д/1,1/0,3-6/32,5/AЛ | ВДО-630-4/6Д/1,1/0,3-6/32,5/AЛ | 620 мм | 690 мм | 634 мм | 620 мм | 630 мм | 400 мм | 120 мм | 105 мм | 3600.0 л/с | 6 | 355 мм | 1100 Вт | 750 мм | 700 мм | 12 мм | 200 мм | -200 мм | 12 | 310 мм | 42.00 кг | Двигатель : Двигатель_1.1 кВт |
| ВДО-630-4/6Д/1,5/0,37-6/37,5/AЛ | ВДО-630-4/6Д/1,5/0,37-6/37,5/AЛ | 620 мм | 690 мм | 634 мм | 620 мм | 630 мм | 400 мм | 120 мм | 105 мм | 3850.0 л/с | 6 | 355 мм | 1500 Вт | 750 мм | 700 мм | 12 мм | 200 мм | -200 мм | 12 | 310 мм | 46.00 кг | Двигатель : Двигатель_1.5 кВт |
| ВДО-630-4/6Д/2,2/0,7-6/45/AЛ | ВДО-630-4/6Д/2,2/0,7-6/45/AЛ | 620 мм | 690 мм | 634 мм | 620 мм | 630 мм | 500 мм | 150 мм | 135 мм | 4350.0 л/с | 6 | 355 мм | 2200 Вт | 750 мм | 700 мм | 12 мм | 250 мм | -250 мм | 12 | 310 мм | 57.00 кг | Двигатель : Двигатель_2.2 кВт |
| ВДО-630-4/8Д/0,6/0,15-8/25/AЛ | ВДО-630-4/8Д/0,6/0,15-8/25/AЛ | 620 мм | 690 мм | 634 мм | 620 мм | 630 мм | 400 мм | 120 мм | 105 мм | 1800.0 л/с | 8 | 355 мм | 600 Вт | 750 мм | 700 мм | 12 мм | 200 мм | -200 мм | 12 | 310 мм | 38.00 кг | Двигатель : Двигатель_0.55 кВт |
| ВДО-630-4/8Д/0,6/0,15-8/30/AЛ | ВДО-630-4/8Д/0,6/0,15-8/30/AЛ | 620 мм | 690 мм | 634 мм | 620 мм | 630 мм | 400 мм | 120 мм | 105 мм | 2200.0 л/с | 8 | 355 мм | 600 Вт | 750 мм | 700 мм | 12 мм | 200 мм | -200 мм | 12 | 310 мм | 38.00 кг | Двигатель : Двигатель_0.55 кВт |
| ВДО-630-4/8Д/0,8/0,2-8/35/AЛ | ВДО-630-4/8Д/0,8/0,2-8/35/AЛ | 620 мм | 690 мм | 634 мм | 620 мм | 630 мм | 400 мм | 120 мм | 105 мм | 2800.0 л/с | 8 | 355 мм | 800 Вт | 750 мм | 700 мм | 12 мм | 200 мм | -200 мм | 12 | 310 мм | 38.00 кг | Двигатель : Двигатель_0.75 кВт |
| ВДО-630-4/8Д/1,2/0,3-8/40/AЛ | ВДО-630-4/8Д/1,2/0,3-8/40/AЛ | 620 мм | 690 мм | 634 мм | 620 мм | 630 мм | 400 мм | 120 мм | 105 мм | 3200.0 л/с | 8 | 355 мм | 1200 Вт | 750 мм | 700 мм | 12 мм | 200 мм | -200 мм | 12 | 310 мм | 43.50 кг | Двигатель : Двигатель_1.1 кВт |
| ВДО-630-4/8Д/1,2/0,3-6/32,5/AЛ | ВДО-630-4/8Д/1,2/0,3-6/32,5/AЛ | 620 мм | 690 мм | 634 мм | 620 мм | 630 мм | 400 мм | 120 мм | 105 мм | 3600.0 л/с | 6 | 355 мм | 1200 Вт | 750 мм | 700 мм | 12 мм | 200 мм | -200 мм | 12 | 310 мм | 46.00 кг | Двигатель : Двигатель_1.1 кВт |
| ВДО-630-4/8Д/1,6/0,4-6/37,5/AЛ | ВДО-630-4/8Д/1,6/0,4-6/37,5/AЛ | 620 мм | 690 мм | 634 мм | 620 мм | 630 мм | 400 мм | 120 мм | 105 мм | 3900.0 л/с | 6 | 355 мм | 1600 Вт | 750 мм | 700 мм | 12 мм | 200 мм | -200 мм | 12 | 310 мм | 49.00 кг | Двигатель : Двигатель_1.5 кВт |
| ВДО-630-4/8Д/2,2/0,55-6/45/AЛ | ВДО-630-4/8Д/2,2/0,55-6/45/AЛ | 620 мм | 690 мм | 634 мм | 620 мм | 630 мм | 500 мм | 150 мм | 135 мм | 4350.0 л/с | 6 | 355 мм | 2200 Вт | 750 мм | 700 мм | 12 мм | 250 мм | -250 мм | 12 | 310 мм | 60.00 кг | Двигатель : Двигатель_2.2 кВт |
| ВДО-710-4Д/1,1-6/25/AЛ | ВДО-710-4Д/1,1-6/25/AЛ | 770 мм | 810 мм | 714 мм | 700 мм | 710 мм | 400 мм | 120 мм | 105 мм | 3900.0 л/с | 6 | 395 мм | 1100 Вт | 845 мм | 795 мм | 12 мм | 200 мм | -200 мм | 16 | 385 мм | 51.50 кг | Двигатель : Двигатель_1.1 кВт |
| ВДО-710-4Д/1,5-6/30/AЛ | ВДО-710-4Д/1,5-6/30/AЛ | 770 мм | 810 мм | 714 мм | 700 мм | 710 мм | 400 мм | 120 мм | 105 мм | 4550.0 л/с | 6 | 395 мм | 1500 Вт | 845 мм | 795 мм | 12 мм | 200 мм | -200 мм | 16 | 385 мм | 55.00 кг | Двигатель : Двигатель_1.5 кВт |
| ВДО-710-4Д/2,2-6/35/AЛ | ВДО-710-4Д/2,2-6/35/AЛ | 770 мм | 810 мм | 714 мм | 700 мм | 710 мм | 400 мм | 120 мм | 105 мм | 5250.0 л/с | 6 | 395 мм | 2200 Вт | 845 мм | 795 мм | 12 мм | 200 мм | -200 мм | 16 | 385 мм | 61.00 кг | Двигатель : Двигатель_2.2 кВт |
| ВДО-710-4Д/2,2-6/40/AЛ | ВДО-710-4Д/2,2-6/40/AЛ | 770 мм | 810 мм | 714 мм | 700 мм | 710 мм | 400 мм | 120 мм | 105 мм | 5500.0 л/с | 6 | 395 мм | 2200 Вт | 845 мм | 795 мм | 12 мм | 200 мм | -200 мм | 16 | 385 мм | 61.00 кг | Двигатель : Двигатель_2.2 кВт |
| ВДО-710-4Д/3-6/45/AЛ | ВДО-710-4Д/3-6/45/AЛ | 770 мм | 810 мм | 714 мм | 700 мм | 710 мм | 500 мм | 150 мм | 135 мм | 6100.0 л/с | 6 | 395 мм | 3000 Вт | 845 мм | 795 мм | 12 мм | 250 мм | -250 мм | 16 | 385 мм | 75.00 кг | Двигатель : Двигатель_3 кВт |
| ВДО-710-6Д/0,25-6/20/AЛ | ВДО-710-6Д/0,25-6/20/AЛ | 770 мм | 810 мм | 714 мм | 700 мм | 710 мм | 400 мм | 120 мм | 105 мм | 2000.0 л/с | 6 | 395 мм | 250 Вт | 845 мм | 795 мм | 12 мм | 200 мм | -200 мм | 16 | 385 мм | 45.50 кг | Двигатель : Двигатель_0.25 кВт |
| ВДО-710-6Д/0,25-6/25/AЛ | ВДО-710-6Д/0,25-6/25/AЛ | 770 мм | 810 мм | 714 мм | 700 мм | 710 мм | 400 мм | 120 мм | 105 мм | 2500.0 л/с | 6 | 395 мм | 250 Вт | 845 мм | 795 мм | 12 мм | 200 мм | -200 мм | 16 | 385 мм | 45.50 кг | Двигатель : Двигатель_0.25 кВт |
| ВДО-710-6Д/0,37-6/30/AЛ | ВДО-710-6Д/0,37-6/30/AЛ | 770 мм | 810 мм | 714 мм | 700 мм | 710 мм | 400 мм | 120 мм | 105 мм | 3000.0 л/с | 6 | 395 мм | 370 Вт | 845 мм | 795 мм | 12 мм | 200 мм | -200 мм | 16 | 385 мм | 49.50 кг | Двигатель : Двигатель_0.37 кВт |
| ВДО-710-6Д/0,55-6/35/AЛ | ВДО-710-6Д/0,55-6/35/AЛ | 770 мм | 810 мм | 714 мм | 700 мм | 710 мм | 400 мм | 120 мм | 105 мм | 3500.0 л/с | 6 | 395 мм | 550 Вт | 845 мм | 795 мм | 12 мм | 200 мм | -200 мм | 16 | 385 мм | 53.00 кг | Двигатель : Двигатель_0.55 кВт |
| ВДО-710-6Д/0,75-6/40/AЛ | ВДО-710-6Д/0,75-6/40/AЛ | 770 мм | 810 мм | 714 мм | 700 мм | 710 мм | 400 мм | 120 мм | 105 мм | 3650.0 л/с | 6 | 395 мм | 750 Вт | 845 мм | 795 мм | 12 мм | 200 мм | -200 мм | 16 | 385 мм | 56.00 кг | Двигатель : Двигатель_0.75 кВт |
| ВДО-710-6Д/1,1-6/45/AЛ | ВДО-710-6Д/1,1-6/45/AЛ | 770 мм | 810 мм | 714 мм | 700 мм | 710 мм | 400 мм | 120 мм | 105 мм | 4050.0 л/с | 6 | 395 мм | 1100 Вт | 845 мм | 795 мм | 12 мм | 200 мм | -200 мм | 16 | 385 мм | 60.00 кг | Двигатель : Двигатель_1.1 кВт |
| ВДО-710-4/6Д/0,75/0,25-6/20/AЛ | ВДО-710-4/6Д/0,75/0,25-6/20/AЛ | 770 мм | 810 мм | 714 мм | 700 мм | 710 мм | 400 мм | 120 мм | 105 мм | 3000.0 л/с | 6 | 395 мм | 750 Вт | 845 мм | 795 мм | 12 мм | 200 мм | -200 мм | 16 | 385 мм | 49.00 кг | Двигатель : Двигатель_0.75 кВт |
| ВДО-710-4/6Д/1,1/0,3-6/25/AЛ | ВДО-710-4/6Д/1,1/0,3-6/25/AЛ | 770 мм | 810 мм | 714 мм | 700 мм | 710 мм | 400 мм | 120 мм | 105 мм | 3750.0 л/с | 6 | 395 мм | 1100 Вт | 845 мм | 795 мм | 12 мм | 200 мм | -200 мм | 16 | 385 мм | 54.00 кг | Двигатель : Двигатель_1.1 кВт |
| ВДО-710-4/6Д/1,5/0,37-6/30/AЛ | ВДО-710-4/6Д/1,5/0,37-6/30/AЛ | 770 мм | 810 мм | 714 мм | 700 мм | 710 мм | 400 мм | 120 мм | 105 мм | 4550.0 л/с | 6 | 395 мм | 1500 Вт | 845 мм | 795 мм | 12 мм | 200 мм | -200 мм | 16 | 385 мм | 58.00 кг | Двигатель : Двигатель_1.5 кВт |
| ВДО-710-4/6Д/2,2/0,7-6/35/AЛ | ВДО-710-4/6Д/2,2/0,7-6/35/AЛ | 770 мм | 810 мм | 714 мм | 700 мм | 710 мм | 500 мм | 150 мм | 135 мм | 5150.0 л/с | 6 | 395 мм | 2200 Вт | 845 мм | 795 мм | 12 мм | 250 мм | -250 мм | 16 | 385 мм | 72.00 кг | Двигатель : Двигатель_2.2 кВт |
| ВДО-710-4/6Д/2,2/0,7-6/40/AЛ | ВДО-710-4/6Д/2,2/0,7-6/40/AЛ | 770 мм | 810 мм | 714 мм | 700 мм | 710 мм | 500 мм | 150 мм | 135 мм | 5450.0 л/с | 6 | 395 мм | 2200 Вт | 845 мм | 795 мм | 12 мм | 250 мм | -250 мм | 16 | 385 мм | 72.00 кг | Двигатель : Двигатель_2.2 кВт |
| ВДО-710-4/6Д/3/1-6/45/AЛ | ВДО-710-4/6Д/3/1-6/45/AЛ | 770 мм | 810 мм | 714 мм | 700 мм | 710 мм | 500 мм | 150 мм | 135 мм | 6050.0 л/с | 6 | 395 мм | 3000 Вт | 845 мм | 795 мм | 12 мм | 250 мм | -250 мм | 16 | 385 мм | 81.00 кг | Двигатель : Двигатель_3 кВт |
| ВДО-710-4/8Д/0,8/0,2-6/20/AЛ | ВДО-710-4/8Д/0,8/0,2-6/20/AЛ | 770 мм | 810 мм | 714 мм | 700 мм | 710 мм | 400 мм | 120 мм | 105 мм | 3000.0 л/с | 6 | 395 мм | 800 Вт | 845 мм | 795 мм | 12 мм | 200 мм | -200 мм | 16 | 385 мм | 52.00 кг | Двигатель : Двигатель_0.8 кВт |
| ВДО-710-4/8Д/1,2/0,3-6/25/AЛ | ВДО-710-4/8Д/1,2/0,3-6/25/AЛ | 770 мм | 810 мм | 714 мм | 700 мм | 710 мм | 400 мм | 120 мм | 105 мм | 3800.0 л/с | 6 | 395 мм | 1200 Вт | 845 мм | 795 мм | 12 мм | 200 мм | -200 мм | 16 | 385 мм | 58.00 кг | Двигатель : Двигатель_1.1 кВт |
| ВДО-710-4/8Д/1,6/0,4-6/30/AЛ | ВДО-710-4/8Д/1,6/0,4-6/30/AЛ | 770 мм | 810 мм | 714 мм | 700 мм | 710 мм | 400 мм | 120 мм | 105 мм | 4550.0 л/с | 6 | 395 мм | 1600 Вт | 845 мм | 795 мм | 12 мм | 200 мм | -200 мм | 16 | 385 мм | 61.00 кг | Двигатель : Двигатель_1.5 кВт |
| ВДО-710-4/8Д/2,2/0,55-6/35/AЛ | ВДО-710-4/8Д/2,2/0,55-6/35/AЛ | 770 мм | 810 мм | 714 мм | 700 мм | 710 мм | 500 мм | 150 мм | 135 мм | 5150.0 л/с | 6 | 395 мм | 2200 Вт | 845 мм | 795 мм | 12 мм | 250 мм | -250 мм | 16 | 385 мм | 75.00 кг | Двигатель : Двигатель_2.2 кВт |
| ВДО-710-4/8Д/2,2/0,55-6/40/AЛ | ВДО-710-4/8Д/2,2/0,55-6/40/AЛ | 770 мм | 810 мм | 714 мм | 700 мм | 710 мм | 500 мм | 150 мм | 135 мм | 5500.0 л/с | 6 | 395 мм | 2200 Вт | 845 мм | 795 мм | 12 мм | 250 мм | -250 мм | 16 | 385 мм | 75.00 кг | Двигатель : Двигатель_2.2 кВт |
| ВДО-710-4/8Д/2,8/0,7-6/45/AЛ | ВДО-710-4/8Д/2,8/0,7-6/45/AЛ | 770 мм | 810 мм | 714 мм | 700 мм | 710 мм | 500 мм | 150 мм | 135 мм | 6050.0 л/с | 6 | 395 мм | 2800 Вт | 845 мм | 795 мм | 12 мм | 250 мм | -250 мм | 16 | 385 мм | 78.00 кг | Двигатель : Двигатель_2.8 кВт |
| ВДО-800-4Д/1,5-6/25/AЛ | ВДО-800-4Д/1,5-6/25/AЛ | 860 мм | 900 мм | 804 мм | 790 мм | 800 мм | 400 мм | 120 мм | 105 мм | 5000.0 л/с | 6 | 440 мм | 1500 Вт | 925 мм | 875 мм | 12 мм | 200 мм | -200 мм | 16 | 430 мм | 65.50 кг | Двигатель : Двигатель_1.5 кВт |
| ВДО-800-4Д/2,2-6/30/AЛ | ВДО-800-4Д/2,2-6/30/AЛ | 860 мм | 900 мм | 804 мм | 790 мм | 800 мм | 400 мм | 120 мм | 105 мм | 5850.0 л/с | 6 | 440 мм | 2200 Вт | 925 мм | 875 мм | 12 мм | 200 мм | -200 мм | 16 | 430 мм | 65.50 кг | Двигатель : Двигатель_2.2 кВт |
| ВДО-800-4Д/3-6/32,5/AЛ | ВДО-800-4Д/3-6/32,5/AЛ | 860 мм | 900 мм | 804 мм | 790 мм | 800 мм | 500 мм | 150 мм | 135 мм | 6400.0 л/с | 6 | 440 мм | 3000 Вт | 925 мм | 875 мм | 12 мм | 250 мм | -250 мм | 16 | 430 мм | 80.00 кг | Двигатель : Двигатель_3 кВт |
| ВДО-800-4Д/3-6/35/AЛ | ВДО-800-4Д/3-6/35/AЛ | 860 мм | 900 мм | 804 мм | 790 мм | 800 мм | 500 мм | 150 мм | 135 мм | 7000.0 л/с | 6 | 440 мм | 3000 Вт | 925 мм | 875 мм | 12 мм | 250 мм | -250 мм | 16 | 430 мм | 80.00 кг | Двигатель : Двигатель_3 кВт |
| ВДО-800-4Д/4-6/37,5/AЛ | ВДО-800-4Д/4-6/37,5/AЛ | 860 мм | 900 мм | 804 мм | 790 мм | 800 мм | 500 мм | 150 мм | 135 мм | 7250.0 л/с | 6 | 440 мм | 4000 Вт | 925 мм | 875 мм | 12 мм | 250 мм | -250 мм | 16 | 430 мм | 85.00 кг | Двигатель : Двигатель_4 кВт |
| ВДО-800-4Д/4-6/40/AЛ | ВДО-800-4Д/4-6/40/AЛ | 860 мм | 900 мм | 804 мм | 790 мм | 800 мм | 500 мм | 150 мм | 135 мм | 7500.0 л/с | 6 | 440 мм | 4000 Вт | 925 мм | 875 мм | 12 мм | 250 мм | -250 мм | 16 | 430 мм | 85.00 кг | Двигатель : Двигатель_4 кВт |
| ВДО-800-4Д/5,5-6/45/AЛ | ВДО-800-4Д/5,5-6/45/AЛ | 860 мм | 900 мм | 804 мм | 790 мм | 800 мм | 550 мм | 165 мм | 150 мм | 8000.0 л/с | 6 | 440 мм | 5500 Вт | 925 мм | 875 мм | 12 мм | 275 мм | -275 мм | 16 | 430 мм | 104.00 кг | Двигатель : Двигатель_5.5 кВт |
| ВДО-800-6Д/0,37-6/20/AЛ | ВДО-800-6Д/0,37-6/20/AЛ | 860 мм | 900 мм | 804 мм | 790 мм | 800 мм | 400 мм | 120 мм | 105 мм | 2500.0 л/с | 6 | 440 мм | 370 Вт | 925 мм | 875 мм | 12 мм | 200 мм | -200 мм | 16 | 430 мм | 53.50 кг | Двигатель : Двигатель_0.37 кВт |
| ВДО-800-6Д/0,55-6/25/AЛ | ВДО-800-6Д/0,55-6/25/AЛ | 860 мм | 900 мм | 804 мм | 790 мм | 800 мм | 400 мм | 120 мм | 105 мм | 3300.0 л/с | 6 | 440 мм | 550 Вт | 925 мм | 875 мм | 12 мм | 200 мм | -200 мм | 16 | 430 мм | 56.50 кг | Двигатель : Двигатель_0.55 кВт |
| ВДО-800-6Д/0,75-6/30/AЛ | ВДО-800-6Д/0,75-6/30/AЛ | 860 мм | 900 мм | 804 мм | 790 мм | 800 мм | 400 мм | 120 мм | 105 мм | 3900.0 л/с | 6 | 440 мм | 750 Вт | 925 мм | 875 мм | 12 мм | 200 мм | -200 мм | 16 | 430 мм | 60.50 кг | Двигатель : Двигатель_0.75 кВт |
| ВДО-800-6Д/0,75-6/32,5/AЛ | ВДО-800-6Д/0,75-6/32,5/AЛ | 860 мм | 900 мм | 804 мм | 790 мм | 800 мм | 400 мм | 120 мм | 105 мм | 4300.0 л/с | 6 | 440 мм | 750 Вт | 925 мм | 875 мм | 12 мм | 200 мм | -200 мм | 16 | 430 мм | 60.50 кг | Двигатель : Двигатель_0.75 кВт |
| ВДО-800-6Д/1,1-6/35/AЛ | ВДО-800-6Д/1,1-6/35/AЛ | 860 мм | 900 мм | 804 мм | 790 мм | 800 мм | 400 мм | 120 мм | 105 мм | 4400.0 л/с | 6 | 440 мм | 1100 Вт | 925 мм | 875 мм | 12 мм | 200 мм | -200 мм | 16 | 430 мм | 64.50 кг | Двигатель : Двигатель_1.1 кВт |
| ВДО-800-6Д/1,1-6/37,5/AЛ | ВДО-800-6Д/1,1-6/37,5/AЛ | 860 мм | 900 мм | 804 мм | 790 мм | 800 мм | 400 мм | 120 мм | 105 мм | 4700.0 л/с | 6 | 440 мм | 1100 Вт | 925 мм | 875 мм | 12 мм | 200 мм | -200 мм | 16 | 430 мм | 64.50 кг | Двигатель : Двигатель_1.1 кВт |
| ВДО-800-6Д/1,1-6/40/AЛ | ВДО-800-6Д/1,1-6/40/AЛ | 860 мм | 900 мм | 804 мм | 790 мм | 800 мм | 400 мм | 120 мм | 105 мм | 5000.0 л/с | 6 | 440 мм | 1100 Вт | 925 мм | 875 мм | 12 мм | 200 мм | -200 мм | 16 | 430 мм | 64.50 кг | Двигатель : Двигатель_1.1 кВт |
| ВДО-800-6Д/1,5-6/45/AЛ | ВДО-800-6Д/1,5-6/45/AЛ | 860 мм | 900 мм | 804 мм | 790 мм | 800 мм | 400 мм | 120 мм | 105 мм | 5300.0 л/с | 6 | 440 мм | 1500 Вт | 925 мм | 875 мм | 12 мм | 200 мм | -200 мм | 16 | 430 мм | 77.00 кг | Двигатель : Двигатель_1.5 кВт |
| ВДО-800-4/6Д/1,1/0,3-6/20/AЛ | ВДО-800-4/6Д/1,1/0,3-6/20/AЛ | 860 мм | 900 мм | 804 мм | 790 мм | 800 мм | 400 мм | 120 мм | 105 мм | 3700.0 л/с | 6 | 440 мм | 1100 Вт | 925 мм | 875 мм | 12 мм | 200 мм | -200 мм | 16 | 430 мм | 58.50 кг | Двигатель : Двигатель_1.1 кВт |
| ВДО-800-4/6Д/1,5/0,37-6/25/AЛ | ВДО-800-4/6Д/1,5/0,37-6/25/AЛ | 860 мм | 900 мм | 804 мм | 790 мм | 800 мм | 400 мм | 120 мм | 105 мм | 4900.0 л/с | 6 | 440 мм | 1500 Вт | 925 мм | 875 мм | 12 мм | 200 мм | -200 мм | 16 | 430 мм | 62.50 кг | Двигатель : Двигатель_1.5 кВт |
| ВДО-800-4/6Д/2,2/0,7-6/30/AЛ | ВДО-800-4/6Д/2,2/0,7-6/30/AЛ | 860 мм | 900 мм | 804 мм | 790 мм | 800 мм | 500 мм | 150 мм | 135 мм | 5800.0 л/с | 6 | 440 мм | 2200 Вт | 925 мм | 875 мм | 12 мм | 250 мм | -250 мм | 16 | 430 мм | 77.00 кг | Двигатель : Двигатель_2.2 кВт |
| ВДО-800-4/6Д/2,2/0,7-6/32,5/AЛ | ВДО-800-4/6Д/2,2/0,7-6/32,5/AЛ | 860 мм | 900 мм | 804 мм | 790 мм | 800 мм | 500 мм | 150 мм | 135 мм | 6400.0 л/с | 6 | 440 мм | 2200 Вт | 925 мм | 875 мм | 12 мм | 250 мм | -250 мм | 16 | 430 мм | 77.00 кг | Двигатель : Двигатель_2.2 кВт |
| ВДО-800-4/6Д/3/1-6/35/AЛ | ВДО-800-4/6Д/3/1-6/35/AЛ | 860 мм | 900 мм | 804 мм | 790 мм | 800 мм | 500 мм | 150 мм | 135 мм | 6900.0 л/с | 6 | 440 мм | 3000 Вт | 925 мм | 875 мм | 12 мм | 250 мм | -250 мм | 16 | 430 мм | 88.00 кг | Двигатель : Двигатель_3 кВт |
| ВДО-800-4/6Д/3/1-6/37,5/AЛ | ВДО-800-4/6Д/3/1-6/37,5/AЛ | 860 мм | 900 мм | 804 мм | 790 мм | 800 мм | 500 мм | 150 мм | 135 мм | 7200.0 л/с | 6 | 440 мм | 3000 Вт | 925 мм | 875 мм | 12 мм | 250 мм | -250 мм | 16 | 430 мм | 88.00 кг | Двигатель : Двигатель_3 кВт |
| ВДО-800-4/6Д/4,5/1,5-6/45/AЛ | ВДО-800-4/6Д/4,5/1,5-6/45/AЛ | 860 мм | 900 мм | 804 мм | 790 мм | 800 мм | 550 мм | 165 мм | 150 мм | 7200.0 л/с | 6 | 440 мм | 4500 Вт | 925 мм | 875 мм | 12 мм | 275 мм | -275 мм | 16 | 430 мм | 125.00 кг | Двигатель : Двигатель_4.4 кВт |
| ВДО-800-4/8Д/1,2/0,3-6/20/AЛ | ВДО-800-4/8Д/1,2/0,3-6/20/AЛ | 860 мм | 900 мм | 804 мм | 790 мм | 800 мм | 400 мм | 120 мм | 105 мм | 3800.0 л/с | 6 | 440 мм | 1200 Вт | 925 мм | 875 мм | 12 мм | 200 мм | -200 мм | 16 | 430 мм | 62.50 кг | Двигатель : Двигатель_1.1 кВт |
| ВДО-800-4/8Д/1,6/0,4-6/25/AЛ | ВДО-800-4/8Д/1,6/0,4-6/25/AЛ | 860 мм | 900 мм | 804 мм | 790 мм | 800 мм | 400 мм | 120 мм | 105 мм | 5000.0 л/с | 6 | 440 мм | 1600 Вт | 925 мм | 875 мм | 12 мм | 200 мм | -200 мм | 16 | 430 мм | 65.50 кг | Двигатель : Двигатель_1.5 кВт |
| ВДО-800-4/8Д/2,2/0,55-6/30/AЛ | ВДО-800-4/8Д/2,2/0,55-6/30/AЛ | 860 мм | 900 мм | 804 мм | 790 мм | 800 мм | 500 мм | 150 мм | 135 мм | 5800.0 л/с | 6 | 440 мм | 2200 Вт | 925 мм | 875 мм | 12 мм | 250 мм | -250 мм | 16 | 430 мм | 80.00 кг | Двигатель : Двигатель_2.2 кВт |
| ВДО-800-4/8Д/2,8/0,7-6/32,5/AЛ | ВДО-800-4/8Д/2,8/0,7-6/32,5/AЛ | 860 мм | 900 мм | 804 мм | 790 мм | 800 мм | 500 мм | 150 мм | 135 мм | 6350.0 л/с | 6 | 440 мм | 2800 Вт | 925 мм | 875 мм | 12 мм | 250 мм | -250 мм | 16 | 430 мм | 83.00 кг | Двигатель : Двигатель_2.8 кВт |
| ВДО-800-4/8Д/2,8/0,7-6/35/AЛ | ВДО-800-4/8Д/2,8/0,7-6/35/AЛ | 860 мм | 900 мм | 804 мм | 790 мм | 800 мм | 500 мм | 150 мм | 135 мм | 6900.0 л/с | 6 | 440 мм | 2800 Вт | 925 мм | 875 мм | 12 мм | 250 мм | -250 мм | 16 | 430 мм | 83.00 кг | Двигатель : Двигатель_2.8 кВт |
| ВДО-800-4/8Д/3,8/1-6/37,5/AЛ | ВДО-800-4/8Д/3,8/1-6/37,5/AЛ | 860 мм | 900 мм | 804 мм | 790 мм | 800 мм | 500 мм | 150 мм | 135 мм | 7200.0 л/с | 6 | 440 мм | 3800 Вт | 925 мм | 875 мм | 12 мм | 250 мм | -250 мм | 16 | 430 мм | 95.00 кг | Двигатель : Двигатель_4 кВт |
| ВДО-800-4/8Д/3,8/1-6/40/AЛ | ВДО-800-4/8Д/3,8/1-6/40/AЛ | 860 мм | 900 мм | 804 мм | 790 мм | 800 мм | 500 мм | 150 мм | 135 мм | 7500.0 л/с | 6 | 440 мм | 3800 Вт | 925 мм | 875 мм | 12 мм | 250 мм | -250 мм | 16 | 430 мм | 95.00 кг | Двигатель : Двигатель_4 кВт |
| ВДО-800-4/8Д/5/1,3-6/45/AЛ | ВДО-800-4/8Д/5/1,3-6/45/AЛ | 860 мм | 900 мм | 804 мм | 790 мм | 800 мм | 550 мм | 165 мм | 150 мм | 8000.0 л/с | 6 | 440 мм | 5000 Вт | 925 мм | 875 мм | 12 мм | 275 мм | -275 мм | 16 | 430 мм | 125.00 кг | Двигатель : Двигатель_5 кВт |
| ВДО-900-4Д/4-8/28,5/AЛ | ВДО-900-4Д/4-8/28,5/AЛ | 970 мм | 1015 мм | 904 мм | 890 мм | 900 мм | 550 мм | 165 мм | 150 мм | 7800.0 л/с | 8 | 490 мм | 4000 Вт | 1025 мм | 975 мм | 15 мм | 275 мм | -275 мм | 16 | 485 мм | 97.00 кг | Двигатель : Двигатель_4 кВт |
| ВДО-900-4Д/5,5-8/33,5/AЛ | ВДО-900-4Д/5,5-8/33,5/AЛ | 970 мм | 1015 мм | 904 мм | 890 мм | 900 мм | 600 мм | 180 мм | 165 мм | 9200.0 л/с | 8 | 490 мм | 5500 Вт | 1025 мм | 975 мм | 15 мм | 300 мм | -300 мм | 16 | 485 мм | 132.50 кг | Двигатель : Двигатель_5.5 кВт |
| ВДО-900-4Д/7,5-8/40/AЛ | ВДО-900-4Д/7,5-8/40/AЛ | 970 мм | 1015 мм | 904 мм | 890 мм | 900 мм | 600 мм | 180 мм | 165 мм | 10500.0 л/с | 8 | 490 мм | 7500 Вт | 1025 мм | 975 мм | 15 мм | 300 мм | -300 мм | 16 | 485 мм | 150.00 кг | Двигатель : Двигатель_7.5 кВт |
| ВДО-900-4Д/11-8/45/AЛ | ВДО-900-4Д/11-8/45/AЛ | 970 мм | 1015 мм | 904 мм | 890 мм | 900 мм | 600 мм | 180 мм | 165 мм | 11700.0 л/с | 8 | 490 мм | 11000 Вт | 1025 мм | 975 мм | 15 мм | 300 мм | -300 мм | 16 | 485 мм | 168.50 кг | Двигатель : Двигатель_11 кВт |
| ВДО-900-6Д/0,75-8/23,5/AЛ | ВДО-900-6Д/0,75-8/23,5/AЛ | 970 мм | 1015 мм | 904 мм | 890 мм | 900 мм | 450 мм | 135 мм | 120 мм | 4200.0 л/с | 8 | 490 мм | 750 Вт | 1025 мм | 975 мм | 15 мм | 225 мм | -225 мм | 16 | 485 мм | 71.50 кг | Двигатель : Двигатель_0.75 кВт |
| ВДО-900-6Д/1,1-8/28,5/AЛ | ВДО-900-6Д/1,1-8/28,5/AЛ | 970 мм | 1015 мм | 904 мм | 890 мм | 900 мм | 450 мм | 135 мм | 120 мм | 5250.0 л/с | 8 | 490 мм | 1100 Вт | 1025 мм | 975 мм | 15 мм | 225 мм | -225 мм | 16 | 485 мм | 75.50 кг | Двигатель : Двигатель_1.1 кВт |
| ВДО-900-6Д/1,5-8/33,5/AЛ | ВДО-900-6Д/1,5-8/33,5/AЛ | 970 мм | 1015 мм | 904 мм | 890 мм | 900 мм | 550 мм | 165 мм | 150 мм | 6100.0 л/с | 8 | 490 мм | 1500 Вт | 1025 мм | 975 мм | 15 мм | 275 мм | -275 мм | 16 | 485 мм | 89.00 кг | Двигатель : Двигатель_1.5 кВт |
| ВДО-900-6Д/2,2-8/41/AЛ | ВДО-900-6Д/2,2-8/41/AЛ | 970 мм | 1015 мм | 904 мм | 890 мм | 900 мм | 550 мм | 165 мм | 150 мм | 7100.0 л/с | 8 | 490 мм | 2200 Вт | 1025 мм | 975 мм | 15 мм | 275 мм | -275 мм | 16 | 485 мм | 101.00 кг | Двигатель : Двигатель_2.2 кВт |
| ВДО-900-6Д/3-8/45/AЛ | ВДО-900-6Д/3-8/45/AЛ | 970 мм | 1015 мм | 904 мм | 890 мм | 900 мм | 600 мм | 180 мм | 165 мм | 7650.0 л/с | 8 | 490 мм | 3000 Вт | 1025 мм | 975 мм | 15 мм | 300 мм | -300 мм | 16 | 485 мм | 104.50 кг | Двигатель : Двигатель_3 кВт |
| ВДО-900-4/6Д/3/1-8/23,5/AЛ | ВДО-900-4/6Д/3/1-8/23,5/AЛ | 970 мм | 1015 мм | 904 мм | 890 мм | 900 мм | 550 мм | 165 мм | 150 мм | 6400.0 л/с | 8 | 490 мм | 3000 Вт | 1025 мм | 975 мм | 15 мм | 275 мм | -275 мм | 16 | 485 мм | 100.00 кг | Двигатель : Двигатель_3 кВт |
| ВДО-900-4/6Д/4,5/1,5-8/28,5/AЛ | ВДО-900-4/6Д/4,5/1,5-8/28,5/AЛ | 970 мм | 1015 мм | 904 мм | 890 мм | 900 мм | 600 мм | 180 мм | 165 мм | 7800.0 л/с | 8 | 490 мм | 4500 Вт | 1025 мм | 975 мм | 15 мм | 300 мм | -300 мм | 16 | 485 мм | 153.50 кг | Двигатель : Двигатель_4.4 кВт |
| ВДО-900-4/6Д/6/2,2-8/33,5/AЛ | ВДО-900-4/6Д/6/2,2-8/33,5/AЛ | 970 мм | 1015 мм | 904 мм | 890 мм | 900 мм | 600 мм | 180 мм | 165 мм | 9000.0 л/с | 8 | 490 мм | 6000 Вт | 1025 мм | 975 мм | 15 мм | 300 мм | -300 мм | 16 | 485 мм | 164.50 кг | Двигатель : Двигатель_6 кВт |
| ВДО-900-4/6Д/10/3,3-8/45/AЛ | ВДО-900-4/6Д/10/3,3-8/45/AЛ | 970 мм | 1015 мм | 904 мм | 890 мм | 900 мм | 750 мм | 225 мм | 210 мм | 11500.0 л/с | 8 | 490 мм | 10000 Вт | 1025 мм | 975 мм | 15 мм | 375 мм | -375 мм | 17 | 485 мм | 227.50 кг | Двигатель : Двигатель_11 кВт |
| ВДО-900-4/8Д/2,8/0,7-8/23,5/AЛ | ВДО-900-4/8Д/2,8/0,7-8/23,5/AЛ | 970 мм | 1015 мм | 904 мм | 890 мм | 900 мм | 550 мм | 165 мм | 150 мм | 6500.0 л/с | 8 | 490 мм | 2800 Вт | 1025 мм | 975 мм | 15 мм | 275 мм | -275 мм | 17 | 485 мм | 95.00 кг | Двигатель : Двигатель_2.8 кВт |
| ВДО-900-4/8Д/3,8/1-8/28,5/AЛ | ВДО-900-4/8Д/3,8/1-8/28,5/AЛ | 970 мм | 1015 мм | 904 мм | 890 мм | 900 мм | 550 мм | 165 мм | 150 мм | 7800.0 л/с | 8 | 490 мм | 3800 Вт | 1025 мм | 975 мм | 15 мм | 275 мм | -275 мм | 17 | 485 мм | 107.00 кг | Двигатель : Двигатель_4 кВт |
| ВДО-900-4/8Д/5/1,3-8/33,5/AЛ | ВДО-900-4/8Д/5/1,3-8/33,5/AЛ | 970 мм | 1015 мм | 904 мм | 890 мм | 900 мм | 600 мм | 180 мм | 165 мм | 9100.0 л/с | 8 | 490 мм | 5000 Вт | 1025 мм | 975 мм | 15 мм | 300 мм | -300 мм | 17 | 485 мм | 153.50 кг | Двигатель : Двигатель_5 кВт |
| ВДО-900-4/8Д/7,2/1,8-8/40/AЛ | ВДО-900-4/8Д/7,2/1,8-8/40/AЛ | 970 мм | 1015 мм | 904 мм | 890 мм | 900 мм | 600 мм | 180 мм | 165 мм | 10500.0 л/с | 8 | 490 мм | 7200 Вт | 1025 мм | 975 мм | 15 мм | 300 мм | -300 мм | 17 | 485 мм | 165.50 кг | Двигатель : Двигатель_7.5 кВт |
| ВДО-900-4/8Д/11/3-8/45/AЛ | ВДО-900-4/8Д/11/3-8/45/AЛ | 970 мм | 1015 мм | 904 мм | 890 мм | 900 мм | 750 мм | 225 мм | 210 мм | 11500.0 л/с | 8 | 490 мм | 11000 Вт | 1025 мм | 975 мм | 15 мм | 375 мм | -375 мм | 17 | 485 мм | 226.50 кг | Двигатель : Двигатель_11 кВт |
| ВДО-1000-4Д/7,5-6/30/AЛ | ВДО-1000-4Д/7,5-6/30/AЛ | 1070 мм | 1115 мм | 1004 мм | 990 мм | 1000 мм | 600 мм | 180 мм | 165 мм | 12600.0 л/с | 6 | 540 мм | 7500 Вт | 1140 мм | 1090 мм | 15 мм | 300 мм | -300 мм | 16 | 535 мм | 165.00 кг | Двигатель : Двигатель_7.5 кВт |
| ВДО-1000-4Д/9,2-6/33/AЛ | ВДО-1000-4Д/9,2-6/33/AЛ | 1070 мм | 1115 мм | 1004 мм | 990 мм | 1000 мм | 600 мм | 180 мм | 165 мм | 13900.0 л/с | 6 | 540 мм | 9200 Вт | 1140 мм | 1090 мм | 15 мм | 300 мм | -300 мм | 16 | 535 мм | 170.50 кг | Двигатель : Двигатель_9.2 кВт |
| ВДО-1000-4Д/11-6/36/AЛ | ВДО-1000-4Д/11-6/36/AЛ | 1070 мм | 1115 мм | 1004 мм | 990 мм | 1000 мм | 600 мм | 180 мм | 165 мм | 14700.0 л/с | 6 | 540 мм | 11000 Вт | 1140 мм | 1090 мм | 15 мм | 300 мм | -300 мм | 16 | 535 мм | 183.50 кг | Двигатель : Двигатель_11 кВт |
| ВДО-1000-4Д/15-6/43/AЛ | ВДО-1000-4Д/15-6/43/AЛ | 1070 мм | 1115 мм | 1004 мм | 990 мм | 1000 мм | 750 мм | 225 мм | 210 мм | 16400.0 л/с | 6 | 540 мм | 15000 Вт | 1140 мм | 1090 мм | 15 мм | 375 мм | -375 мм | 16 | 535 мм | 244.00 кг | Двигатель : Двигатель_15 кВт |
| ВДО-1000-4Д/18,5-6/48/AЛ | ВДО-1000-4Д/18,5-6/48/AЛ | 1070 мм | 1115 мм | 1004 мм | 990 мм | 1000 мм | 750 мм | 225 мм | 210 мм | 17200.0 л/с | 6 | 540 мм | 18500 Вт | 1140 мм | 1090 мм | 15 мм | 375 мм | -375 мм | 16 | 535 мм | 259.00 кг | Двигатель : Двигатель_18.5 кВт |
| ВДО-1000-6Д/1,5-6/23/AЛ | ВДО-1000-6Д/1,5-6/23/AЛ | 1070 мм | 1115 мм | 1004 мм | 990 мм | 1000 мм | 550 мм | 165 мм | 150 мм | 6400.0 л/с | 6 | 540 мм | 1500 Вт | 1140 мм | 1090 мм | 15 мм | 275 мм | -275 мм | 16 | 535 мм | 101.00 кг | Двигатель : Двигатель_1.5 кВт |
| ВДО-1000-6Д/2,2-6/29/AЛ | ВДО-1000-6Д/2,2-6/29/AЛ | 1070 мм | 1115 мм | 1004 мм | 990 мм | 1000 мм | 550 мм | 165 мм | 150 мм | 8300.0 л/с | 6 | 540 мм | 2200 Вт | 1140 мм | 1090 мм | 15 мм | 275 мм | -275 мм | 16 | 535 мм | 114.00 кг | Двигатель : Двигатель_2.2 кВт |
| ВДО-1000-6Д/3-6/35/AЛ | ВДО-1000-6Д/3-6/35/AЛ | 1070 мм | 1115 мм | 1004 мм | 990 мм | 1000 мм | 600 мм | 180 мм | 165 мм | 9500.0 л/с | 6 | 540 мм | 3000 Вт | 1140 мм | 1090 мм | 15 мм | 300 мм | -300 мм | 16 | 535 мм | 155.50 кг | Двигатель : Двигатель_3 кВт |
| ВДО-1000-6Д/4-6/41/AЛ | ВДО-1000-6Д/4-6/41/AЛ | 1070 мм | 1115 мм | 1004 мм | 990 мм | 1000 мм | 600 мм | 180 мм | 165 мм | 10500.0 л/с | 6 | 540 мм | 4000 Вт | 1140 мм | 1090 мм | 15 мм | 300 мм | -300 мм | 16 | 535 мм | 159.50 кг | Двигатель : Двигатель_4 кВт |
| ВДО-1000-6Д/5,5-6/48/AЛ | ВДО-1000-6Д/5,5-6/48/AЛ | 1070 мм | 1115 мм | 1004 мм | 990 мм | 1000 мм | 600 мм | 180 мм | 165 мм | 11300.0 л/с | 6 | 540 мм | 5500 Вт | 1140 мм | 1090 мм | 15 мм | 300 мм | -300 мм | 16 | 535 мм | 172.50 кг | Двигатель : Двигатель_5.5 кВт |
| ВДО-1000-4/6Д/4,5/1,5-6/20/AЛ | ВДО-1000-4/6Д/4,5/1,5-6/20/AЛ | 1070 мм | 1115 мм | 1004 мм | 990 мм | 1000 мм | 600 мм | 180 мм | 165 мм | 8600.0 л/с | 6 | 540 мм | 4500 Вт | 1140 мм | 1090 мм | 15 мм | 300 мм | -300 мм | 16 | 535 мм | 168.50 кг | Двигатель : Двигатель_4.4 кВт |
| ВДО-1000-4/6Д/6/2,2-6/25/AЛ | ВДО-1000-4/6Д/6/2,2-6/25/AЛ | 1070 мм | 1115 мм | 1004 мм | 990 мм | 1000 мм | 600 мм | 180 мм | 165 мм | 10800.0 л/с | 6 | 540 мм | 6000 Вт | 1140 мм | 1090 мм | 15 мм | 300 мм | -300 мм | 16 | 535 мм | 179.50 кг | Двигатель : Двигатель_6 кВт |
| ВДО-1000-4/6Д/10/3,3-6/34/AЛ | ВДО-1000-4/6Д/10/3,3-6/34/AЛ | 1070 мм | 1115 мм | 1004 мм | 990 мм | 1000 мм | 750 мм | 225 мм | 210 мм | 14000.0 л/с | 6 | 540 мм | 10000 Вт | 1140 мм | 1090 мм | 15 мм | 375 мм | -375 мм | 16 | 535 мм | 244.50 кг | Двигатель : Двигатель_10 кВт |
| ВДО-1000-4/6Д/14/4,5-6/41/AЛ | ВДО-1000-4/6Д/14/4,5-6/41/AЛ | 1070 мм | 1115 мм | 1004 мм | 990 мм | 1000 мм | 750 мм | 225 мм | 210 мм | 16100.0 л/с | 6 | 540 мм | 14000 Вт | 1140 мм | 1090 мм | 15 мм | 375 мм | -375 мм | 16 | 535 мм | 259.50 кг | Двигатель : Двигатель_14 кВт |
| ВДО-1000-4/6Д/16/6,5-6/45/AЛ | ВДО-1000-4/6Д/16/6,5-6/45/AЛ | 1070 мм | 1115 мм | 1004 мм | 990 мм | 1000 мм | 800 мм | 240 мм | 225 мм | 16800.0 л/с | 6 | 540 мм | 16000 Вт | 1140 мм | 1090 мм | 15 мм | 400 мм | -400 мм | 16 | 535 мм | 328.00 кг | Двигатель : Двигатель_16 кВт |
| ВДО-1000-4/8Д/5/1,3-6/23/AЛ | ВДО-1000-4/8Д/5/1,3-6/23/AЛ | 1070 мм | 1115 мм | 1004 мм | 990 мм | 1000 мм | 600 мм | 180 мм | 165 мм | 9700.0 л/с | 6 | 540 мм | 5000 Вт | 1140 мм | 1090 мм | 15 мм | 300 мм | -300 мм | 16 | 535 мм | 168.50 кг | Двигатель : Двигатель_5 кВт |
| ВДО-1000-4/8Д/7,2/1,8-6/29/AЛ | ВДО-1000-4/8Д/7,2/1,8-6/29/AЛ | 1070 мм | 1115 мм | 1004 мм | 990 мм | 1000 мм | 600 мм | 180 мм | 165 мм | 12500.0 л/с | 6 | 540 мм | 7200 Вт | 1140 мм | 1090 мм | 15 мм | 300 мм | -300 мм | 16 | 535 мм | 180.50 кг | Двигатель : Двигатель_7.5 кВт |
| ВДО-1000-4/8Д/11/3-6/36/AЛ | ВДО-1000-4/8Д/11/3-6/36/AЛ | 1070 мм | 1115 мм | 1004 мм | 990 мм | 1000 мм | 750 мм | 225 мм | 210 мм | 14700.0 л/с | 6 | 540 мм | 11000 Вт | 1140 мм | 1090 мм | 15 мм | 375 мм | -375 мм | 16 | 535 мм | 243.50 кг | Двигатель : Двигатель_11 кВт |
| ВДО-1000-4/8Д/14/3,5-6/41/AЛ | ВДО-1000-4/8Д/14/3,5-6/41/AЛ | 1070 мм | 1115 мм | 1004 мм | 990 мм | 1000 мм | 750 мм | 225 мм | 210 мм | 15800.0 л/с | 6 | 540 мм | 14000 Вт | 1140 мм | 1090 мм | 15 мм | 375 мм | -375 мм | 16 | 535 мм | 259.50 кг | Двигатель : Двигатель_14 кВт |
| ВДО-1000-4/8Д/17/4,3-6/46/AЛ | ВДО-1000-4/8Д/17/4,3-6/46/AЛ | 1070 мм | 1115 мм | 1004 мм | 990 мм | 1000 мм | 800 мм | 240 мм | 225 мм | 16650.0 л/с | 6 | 540 мм | 17000 Вт | 1140 мм | 1090 мм | 15 мм | 400 мм | -400 мм | 16 | 535 мм | 295.00 кг | Двигатель : Двигатель_16 кВт |
| ВДО-1120-4Д/9,2-6/27/AЛ | ВДО-1120-4Д/9,2-6/27/AЛ | 1190 мм | 1270 мм | 1124 мм | 1110 мм | 1120 мм | 600 мм | 180 мм | 165 мм | 15400.0 л/с | 6 | 600 мм | 9200 Вт | 1280 мм | 1230 мм | 15 мм | 300 мм | -300 мм | 20 | 595 мм | 189.00 кг | Двигатель : Двигатель_9.2 кВт |
| ВДО-1120-4Д/11-6/31/AЛ | ВДО-1120-4Д/11-6/31/AЛ | 1190 мм | 1270 мм | 1124 мм | 1110 мм | 1120 мм | 600 мм | 180 мм | 165 мм | 17500.0 л/с | 6 | 600 мм | 11000 Вт | 1280 мм | 1230 мм | 15 мм | 300 мм | -300 мм | 20 | 595 мм | 202.00 кг | Двигатель : Двигатель_11 кВт |
| ВДО-1120-4Д/15-6/35/AЛ | ВДО-1120-4Д/15-6/35/AЛ | 1190 мм | 1270 мм | 1124 мм | 1110 мм | 1120 мм | 750 мм | 225 мм | 210 мм | 18900.0 л/с | 6 | 600 мм | 15000 Вт | 1280 мм | 1230 мм | 15 мм | 375 мм | -375 мм | 20 | 595 мм | 296.00 кг | Двигатель : Двигатель_15 кВт |
| ВДО-1120-4Д/18,5-6/40/AЛ | ВДО-1120-4Д/18,5-6/40/AЛ | 1190 мм | 1270 мм | 1124 мм | 1110 мм | 1120 мм | 750 мм | 225 мм | 210 мм | 20500.0 л/с | 6 | 600 мм | 18500 Вт | 1280 мм | 1230 мм | 15 мм | 375 мм | -375 мм | 20 | 595 мм | 312.00 кг | Двигатель : Двигатель_18.5 кВт |
| ВДО-1120-4Д/22-6/43/AЛ | ВДО-1120-4Д/22-6/43/AЛ | 1190 мм | 1270 мм | 1124 мм | 1110 мм | 1120 мм | 800 мм | 240 мм | 225 мм | 21600.0 л/с | 6 | 600 мм | 22000 Вт | 1280 мм | 1230 мм | 15 мм | 400 мм | -400 мм | 20 | 595 мм | 352.00 кг | Двигатель : Двигатель_20 кВт |
| ВДО-1120-6Д/2,2-6/23/AЛ | ВДО-1120-6Д/2,2-6/23/AЛ | 1190 мм | 1270 мм | 1124 мм | 1110 мм | 1120 мм | 550 мм | 165 мм | 150 мм | 8600.0 л/с | 6 | 600 мм | 2200 Вт | 1280 мм | 1230 мм | 15 мм | 275 мм | -275 мм | 20 | 595 мм | 146.00 кг | Двигатель : Двигатель_2.2 кВт |
| ВДО-1120-6Д/3-6/29/AЛ | ВДО-1120-6Д/3-6/29/AЛ | 1190 мм | 1270 мм | 1124 мм | 1110 мм | 1120 мм | 600 мм | 180 мм | 165 мм | 11100.0 л/с | 6 | 600 мм | 3000 Вт | 1280 мм | 1230 мм | 15 мм | 300 мм | -300 мм | 20 | 595 мм | 174.00 кг | Двигатель : Двигатель_3 кВт |
| ВДО-1120-6Д/4-6/34/AЛ | ВДО-1120-6Д/4-6/34/AЛ | 1190 мм | 1270 мм | 1124 мм | 1110 мм | 1120 мм | 600 мм | 180 мм | 165 мм | 12200.0 л/с | 6 | 600 мм | 4000 Вт | 1280 мм | 1230 мм | 15 мм | 300 мм | -300 мм | 20 | 595 мм | 178.00 кг | Двигатель : Двигатель_4 кВт |
| ВДО-1120-6Д/5,5-6/40/AЛ | ВДО-1120-6Д/5,5-6/40/AЛ | 1190 мм | 1270 мм | 1124 мм | 1110 мм | 1120 мм | 600 мм | 180 мм | 165 мм | 13900.0 л/с | 6 | 600 мм | 5500 Вт | 1280 мм | 1230 мм | 15 мм | 300 мм | -300 мм | 20 | 595 мм | 191.00 кг | Двигатель : Двигатель_5.5 кВт |
| ВДО-1120-6Д/7,5-6/46/AЛ | ВДО-1120-6Д/7,5-6/46/AЛ | 1190 мм | 1270 мм | 1124 мм | 1110 мм | 1120 мм | 750 мм | 225 мм | 210 мм | 14700.0 л/с | 6 | 600 мм | 7500 Вт | 1280 мм | 1230 мм | 15 мм | 375 мм | -375 мм | 20 | 595 мм | 280.00 кг | Двигатель : Двигатель_7.5 кВт |
| ВДО-1120-6Д/9,2-6/50/AЛ | ВДО-1120-6Д/9,2-6/50/AЛ | 1190 мм | 1270 мм | 1124 мм | 1110 мм | 1120 мм | 750 мм | 225 мм | 210 мм | 15000.0 л/с | 6 | 600 мм | 9200 Вт | 1280 мм | 1230 мм | 15 мм | 375 мм | -375 мм | 20 | 595 мм | 289.00 кг | Двигатель : Двигатель_9.2 кВт |
| ВДО-1120-4/6Д/6/2,2-5/24/AЛ | ВДО-1120-4/6Д/6/2,2-5/24/AЛ | 1190 мм | 1270 мм | 1124 мм | 1110 мм | 1120 мм | 600 мм | 180 мм | 165 мм | 12500.0 л/с | 6 | 600 мм | 6000 Вт | 1280 мм | 1230 мм | 15 мм | 300 мм | -300 мм | 20 | 595 мм | 196.00 кг | Двигатель : Двигатель_6 кВт |
| ВДО-1120-4/6Д/10/3,3-6/29/AЛ | ВДО-1120-4/6Д/10/3,3-6/29/AЛ | 1190 мм | 1270 мм | 1124 мм | 1110 мм | 1120 мм | 750 мм | 225 мм | 210 мм | 16100.0 л/с | 6 | 600 мм | 10000 Вт | 1280 мм | 1230 мм | 15 мм | 375 мм | -375 мм | 20 | 595 мм | 297.00 кг | Двигатель : Двигатель_10 кВт |
| ВДО-1120-4/6Д/14/4,5-6/34/AЛ | ВДО-1120-4/6Д/14/4,5-6/34/AЛ | 1190 мм | 1270 мм | 1124 мм | 1110 мм | 1120 мм | 750 мм | 225 мм | 210 мм | 18300.0 л/с | 6 | 600 мм | 14000 Вт | 1280 мм | 1230 мм | 15 мм | 375 мм | -375 мм | 20 | 595 мм | 312.00 кг | Двигатель : Двигатель_14 кВт |
| ВДО-1120-4/6Д/16/6,5-6/37/AЛ | ВДО-1120-4/6Д/16/6,5-6/37/AЛ | 1190 мм | 1270 мм | 1124 мм | 1110 мм | 1120 мм | 800 мм | 240 мм | 225 мм | 19400.0 л/с | 6 | 600 мм | 16000 Вт | 1280 мм | 1230 мм | 15 мм | 400 мм | -400 мм | 20 | 595 мм | 384.00 кг | Двигатель : Двигатель_16 кВт |
| ВДО-1120-4/6Д/20/8,5-6/41/AЛ | ВДО-1120-4/6Д/20/8,5-6/41/AЛ | 1190 мм | 1270 мм | 1124 мм | 1110 мм | 1120 мм | 800 мм | 240 мм | 225 мм | 20800.0 л/с | 6 | 600 мм | 20000 Вт | 1280 мм | 1230 мм | 15 мм | 400 мм | -400 мм | 20 | 595 мм | 387.00 кг | Двигатель : Двигатель_20 кВт |
| ВДО-1120-4/8Д/7,2/1,8-6/23/AЛ | ВДО-1120-4/8Д/7,2/1,8-6/23/AЛ | 1190 мм | 1270 мм | 1124 мм | 1110 мм | 1120 мм | 600 мм | 180 мм | 165 мм | 13000.0 л/с | 6 | 600 мм | 7200 Вт | 1280 мм | 1230 мм | 15 мм | 300 мм | -300 мм | 20 | 595 мм | 199.00 кг | Двигатель : Двигатель_7.5 кВт |
| ВДО-1120-4/8Д/11/3-6/31/AЛ | ВДО-1120-4/8Д/11/3-6/31/AЛ | 1190 мм | 1270 мм | 1124 мм | 1110 мм | 1120 мм | 750 мм | 225 мм | 210 мм | 17200.0 л/с | 6 | 600 мм | 11000 Вт | 1280 мм | 1230 мм | 15 мм | 375 мм | -375 мм | 20 | 595 мм | 296.00 кг | Двигатель : Двигатель_11 кВт |
| ВДО-1120-4/8Д/14/3,5-6/34/AЛ | ВДО-1120-4/8Д/14/3,5-6/34/AЛ | 1190 мм | 1270 мм | 1124 мм | 1110 мм | 1120 мм | 750 мм | 225 мм | 210 мм | 18000.0 л/с | 6 | 600 мм | 14000 Вт | 1280 мм | 1230 мм | 15 мм | 375 мм | -375 мм | 20 | 595 мм | 312.00 кг | Двигатель : Двигатель_14 кВт |
| ВДО-1120-4/8Д/17/4,3-6/38/AЛ | ВДО-1120-4/8Д/17/4,3-6/38/AЛ | 1190 мм | 1270 мм | 1124 мм | 1110 мм | 1120 мм | 800 мм | 240 мм | 225 мм | 20000.0 л/с | 6 | 600 мм | 17000 Вт | 1280 мм | 1230 мм | 15 мм | 400 мм | -400 мм | 20 | 595 мм | 351.00 кг | Двигатель : Двигатель_16 кВт |
| ВДО-1120-4/8Д/20/5-6/41/AЛ | ВДО-1120-4/8Д/20/5-6/41/AЛ | 1190 мм | 1270 мм | 1124 мм | 1110 мм | 1120 мм | 800 мм | 240 мм | 225 мм | 20000.0 л/с | 6 | 600 мм | 20000 Вт | 1280 мм | 1230 мм | 15 мм | 400 мм | -400 мм | 20 | 595 мм | 379.00 кг | Двигатель : Двигатель_20 кВт |
| ВДО-1250-4Д/22-8/28/AЛ | ВДО-1250-4Д/22-8/28/AЛ | 1320 мм | 1400 мм | 1254 мм | 1240 мм | 1250 мм | 800 мм | 240 мм | 225 мм | 23900.0 л/с | 8 | 665 мм | 22000 Вт | 1450 мм | 1400 мм | 15 мм | 400 мм | -400 мм | 20 | 660 мм | 377.50 кг | Двигатель : Двигатель_20 кВт |
| ВДО-1250-4Д/30-8/34/AЛ | ВДО-1250-4Д/30-8/34/AЛ | 1320 мм | 1400 мм | 1254 мм | 1240 мм | 1250 мм | 800 мм | 240 мм | 225 мм | 27700.0 л/с | 8 | 665 мм | 30000 Вт | 1450 мм | 1400 мм | 15 мм | 400 мм | -400 мм | 20 | 660 мм | 403.50 кг | Двигатель : Двигатель_28 кВт |
| ВДО-1250-6Д/5,5-8/23/AЛ | ВДО-1250-6Д/5,5-8/23/AЛ | 1320 мм | 1400 мм | 1254 мм | 1240 мм | 1250 мм | 600 мм | 180 мм | 165 мм | 13300.0 л/с | 8 | 665 мм | 5500 Вт | 1450 мм | 1400 мм | 15 мм | 300 мм | -300 мм | 20 | 660 мм | 231.00 кг | Двигатель : Двигатель_5.5 кВт |
| ВДО-1250-6Д/7,5-8/30/AЛ | ВДО-1250-6Д/7,5-8/30/AЛ | 1320 мм | 1400 мм | 1254 мм | 1240 мм | 1250 мм | 750 мм | 225 мм | 210 мм | 16900.0 л/с | 8 | 665 мм | 7500 Вт | 1450 мм | 1400 мм | 15 мм | 375 мм | -375 мм | 20 | 660 мм | 303.00 кг | Двигатель : Двигатель_7.5 кВт |
| ВДО-1250-6Д/9,2-8/34/AЛ | ВДО-1250-6Д/9,2-8/34/AЛ | 1320 мм | 1400 мм | 1254 мм | 1240 мм | 1250 мм | 750 мм | 225 мм | 210 мм | 18600.0 л/с | 8 | 665 мм | 9200 Вт | 1450 мм | 1400 мм | 15 мм | 375 мм | -375 мм | 20 | 660 мм | 303.00 кг | Двигатель : Двигатель_9.2 кВт |
| ВДО-1250-6Д/11-8/38/AЛ | ВДО-1250-6Д/11-8/38/AЛ | 1320 мм | 1400 мм | 1254 мм | 1240 мм | 1250 мм | 750 мм | 225 мм | 210 мм | 20000.0 л/с | 8 | 665 мм | 11000 Вт | 1450 мм | 1400 мм | 15 мм | 375 мм | -375 мм | 20 | 660 мм | 327.00 кг | Двигатель : Двигатель_11 кВт |
| ВДО-1250-4/6Д/16/6,5-8/20/AЛ | ВДО-1250-4/6Д/16/6,5-8/20/AЛ | 1320 мм | 1400 мм | 1254 мм | 1240 мм | 1250 мм | 800 мм | 240 мм | 225 мм | 17500.0 л/с | 8 | 665 мм | 16000 Вт | 1450 мм | 1400 мм | 15 мм | 400 мм | -400 мм | 20 | 660 мм | 408.50 кг | Двигатель : Двигатель_16 кВт |
| ВДО-1250-4/6Д/20/8,5-8/25/AЛ | ВДО-1250-4/6Д/20/8,5-8/25/AЛ | 1320 мм | 1400 мм | 1254 мм | 1240 мм | 1250 мм | 800 мм | 240 мм | 225 мм | 21650.0 л/с | 8 | 665 мм | 20000 Вт | 1450 мм | 1400 мм | 15 мм | 400 мм | -400 мм | 20 | 660 мм | 411.50 кг | Двигатель : Двигатель_20 кВт |
| ВДО-1250-4/6Д/26/9-8/31/AЛ | ВДО-1250-4/6Д/26/9-8/31/AЛ | 1320 мм | 1400 мм | 1254 мм | 1240 мм | 1250 мм | 850 мм | 255 мм | 240 мм | 25800.0 л/с | 8 | 665 мм | 26000 Вт | 1450 мм | 1400 мм | 15 мм | 425 мм | -425 мм | 20 | 660 мм | 510.00 кг | Двигатель : Двигатель_28 кВт |
| ВДО-1250-4/8Д/17/4,3-8/21/AЛ | ВДО-1250-4/8Д/17/4,3-8/21/AЛ | 1320 мм | 1400 мм | 1254 мм | 1240 мм | 1250 мм | 800 мм | 240 мм | 225 мм | 18600.0 л/с | 8 | 665 мм | 17000 Вт | 1450 мм | 1400 мм | 15 мм | 400 мм | -400 мм | 20 | 660 мм | 375.50 кг | Двигатель : Двигатель_16 кВт |
| ВДО-1250-4/8Д/20/5-8/25/AЛ | ВДО-1250-4/8Д/20/5-8/25/AЛ | 1320 мм | 1400 мм | 1254 мм | 1240 мм | 1250 мм | 800 мм | 240 мм | 225 мм | 21600.0 л/с | 8 | 665 мм | 20000 Вт | 1450 мм | 1400 мм | 15 мм | 400 мм | -400 мм | 20 | 660 мм | 403.50 кг | Двигатель : Двигатель_20 кВт |
| ВДО-1250-4/8Д/28/6,5-8/32/AЛ | ВДО-1250-4/8Д/28/6,5-8/32/AЛ | 1320 мм | 1400 мм | 1254 мм | 1240 мм | 1250 мм | 850 мм | 255 мм | 240 мм | 26400.0 л/с | 8 | 665 мм | 28000 Вт | 1450 мм | 1400 мм | 15 мм | 425 мм | -425 мм | 20 | 660 мм | 465.00 кг | Двигатель : Двигатель_28 кВт |
